FCSTD DOCUMENT  (FreeCAD 0.19R24276 (Git))
Label: v5.6_Full
License: All rights reserved
LicenseURL: http://en.wikipedia.org/wiki/All_rights_reserved
objects: App::Link×7, App::DocumentObjectGroup×2, PartDesign::CoordinateSystem×1, App::FeaturePython×1, App::Part×1
note: 1 computed .brp shape members not serialized (recipe doc carries the construction recipe); baked Part::Feature solids carry a one-line shape summary decoded from their .brp
EXTERNAL_REF file=v5.6_Base.FCStd obj=LCS_Origin
EXTERNAL_REF file=v5.6_Base.FCStd obj=Model
EXTERNAL_REF file=v5.6_Base.FCStd obj=LCS_BaseAssembly_Pivot
EXTERNAL_REF file=v5.6_Primary.FCStd obj=LCS_Pivot
EXTERNAL_REF file=v5.6_Primary.FCStd obj=Model
EXTERNAL_REF file=v5.6_Primary.FCStd obj=LCS_SecondaryAssembly
EXTERNAL_REF file=v5.6_Secondary.FCStd obj=LCS_Origin
EXTERNAL_REF file=v5.6_Secondary.FCStd obj=Model
EXTERNAL_REF file=v5.6_Pole.FCStd obj=LCS_Pole_Bottom
EXTERNAL_REF file=v5.6_Primary.FCStd obj=LCS_Primary_Pole_AP
EXTERNAL_REF file=v5.6_Pole.FCStd obj=Model
EXTERNAL_REF file=v5.6_Pole.FCStd obj=LCS_Pole_Top
EXTERNAL_REF file=v5.6_Primary.FCStd obj=LCS_Primary_Pole_FP

FEATURE [App::DocumentObjectGroup] Parts
FEATURE [PartDesign::CoordinateSystem] LCS_Origin
  AttacherType = Attacher::AttachEngine3D
  MapMode = 2
  Support = -> [X_Axis]
FEATURE [App::DocumentObjectGroup] Constraints
FEATURE [App::FeaturePython] Variables  # WARN: FeaturePython — macro-defined, semantics opaque (R4)
  ZDist = 0
FEATURE [App::Link] v5_6_Base
  AssemblyType = Asm4EE
  AttachedBy = #LCS_Origin
  AttachedTo = Parent Assembly#LCS_Origin
  LinkedObject = -> <external v5.6_Base.FCStd>#Model
  expr: Placement = LCS_Origin.Placement * AttachmentOffset * v5_6_Base#LCS_Origin.Placement ^ -1
FEATURE [App::Link] v5_6_Primary
  AssemblyType = Asm4EE
  AttachedBy = #LCS_Pivot
  AttachedTo = v5_6_Base#LCS_BaseAssembly_Pivot
  LinkPlacement = pos=(0,0,135.2) rot=(0,0,1;0rad)
  LinkedObject = -> <external v5.6_Primary.FCStd>#Model
  Placement = pos=(0,0,135.2) rot=(0,0,1;0rad)
  expr: Placement = v5_6_Base.Placement * v5_6_Base#LCS_BaseAssembly_Pivot.Placement * AttachmentOffset * v5_6_Primary#LCS_Pivot.Placement ^ -1
FEATURE [App::Link] v5_6_Secondary
  AssemblyType = Asm4EE
  AttachedBy = #LCS_Origin
  AttachedTo = v5_6_Primary#LCS_SecondaryAssembly
  LinkPlacement = pos=(0,0,969.2) rot=(0,0,1;0rad)
  LinkedObject = -> <external v5.6_Secondary.FCStd>#Model
  Placement = pos=(0,0,969.2) rot=(0,0,1;0rad)
  expr: Placement = v5_6_Primary.Placement * v5_6_Primary#LCS_SecondaryAssembly.Placement * AttachmentOffset * v5_6_Secondary#LCS_Origin.Placement ^ -1
FEATURE [App::Link] Pole_A1
  AssemblyType = Asm4EE
  AttachedBy = #LCS_Pole_Bottom
  AttachedTo = v5_6_Primary#LCS_Primary_Pole_AP
  LinkPlacement = pos=(113,113,84) rot=(0,0,1;0rad)
  LinkedObject = -> <external v5.6_Pole.FCStd>#Model
  Placement = pos=(113,113,84) rot=(0,0,1;0rad)
  expr: Placement = v5_6_Primary.Placement * v5_6_Primary#LCS_Primary_Pole_AP.Placement * AttachmentOffset * v5_6_Pole#LCS_Pole_Bottom.Placement ^ -1
FEATURE [App::Link] Pole_A2
  AssemblyType = Asm4EE
  AttachedBy = #LCS_Pole_Bottom
  AttachedTo = Pole_A1#LCS_Pole_Top
  LinkPlacement = pos=(113,113,592) rot=(0,0,1;0rad)
  LinkedObject = -> <external v5.6_Pole.FCStd>#Model
  Placement = pos=(113,113,592) rot=(0,0,1;0rad)
  expr: Placement = Pole_A1.Placement * v5_6_Pole#LCS_Pole_Top.Placement * AttachmentOffset * v5_6_Pole#LCS_Pole_Bottom.Placement ^ -1
FEATURE [App::Link] Pole_F1
  AssemblyType = Asm4EE
  AttachedBy = #LCS_Pole_Bottom
  AttachedTo = v5_6_Primary#LCS_Primary_Pole_FP
  LinkPlacement = pos=(113,-113,84) rot=(0,0,1;0rad)
  LinkedObject = -> <external v5.6_Pole.FCStd>#Model
  Placement = pos=(113,-113,84) rot=(0,0,1;0rad)
  expr: Placement = v5_6_Primary.Placement * v5_6_Primary#LCS_Primary_Pole_FP.Placement * AttachmentOffset * v5_6_Pole#LCS_Pole_Bottom.Placement ^ -1
FEATURE [App::Link] Pole_F2
  AssemblyType = Asm4EE
  AttachedBy = #LCS_Pole_Bottom
  AttachedTo = Pole_F1#LCS_Pole_Top
  LinkPlacement = pos=(113,-113,592) rot=(0,0,1;0rad)
  LinkedObject = -> <external v5.6_Pole.FCStd>#Model
  Placement = pos=(113,-113,592) rot=(0,0,1;0rad)
  expr: Placement = Pole_F1.Placement * v5_6_Pole#LCS_Pole_Top.Placement * AttachmentOffset * v5_6_Pole#LCS_Pole_Bottom.Placement ^ -1
FEATURE [App::Part] Model
  Configuration = 0
  Group = -> [LCS_Origin,Constraints,Variables,v5_6_Base,v5_6_Primary,v5_6_Secondary,Pole_A1,Pole_A2,Pole_F1,Pole_F2]
  Origin = -> Origin
  Type = Assembly4 Model

RESOLVED EXTERNAL PARTS (link-assembly join: the EXTERNAL_REF files above that resolve inside this repo's crawl, each included once):
---- part v5.6_Base.FCStd = doc fcstd_4a025d0645c7 ----
FCSTD DOCUMENT  (FreeCAD 0.19R24276 (Git))
Label: v5.6_Base
License: All rights reserved
LicenseURL: http://en.wikipedia.org/wiki/All_rights_reserved
objects: App::Link×37, Part::FeaturePython×32, App::DocumentObjectGroup×2, PartDesign::CoordinateSystem×2, App::FeaturePython×1, App::Part×1
note: 34 computed .brp shape members not serialized (recipe doc carries the construction recipe); baked Part::Feature solids carry a one-line shape summary decoded from their .brp
EXTERNAL_REF file=v5.6_Master.FCStd obj=LCS_AFrame_BaseHub
EXTERNAL_REF file=v5.6_Master.FCStd obj=Part002
EXTERNAL_REF file=v5.6_Master.FCStd obj=LCS_AFrame_Corner_AP
EXTERNAL_REF file=v5.6_Master.FCStd obj=Local_CS097
EXTERNAL_REF file=v5.6_Master.FCStd obj=Body038
EXTERNAL_REF file=v5.6_Master.FCStd obj=LCS_AFrame_Corner_FP
EXTERNAL_REF file=v5.6_Master.FCStd obj=LCS_AFrame_Corner_AS
EXTERNAL_REF file=v5.6_Master.FCStd obj=LCS_AFrame_Corner_FS
EXTERNAL_REF file=v5.6_Master.FCStd obj=LCS_AFrame_Post_AP
EXTERNAL_REF file=v5.6_Master.FCStd obj=Local_CS042
EXTERNAL_REF file=v5.6_Master.FCStd obj=Body018
EXTERNAL_REF file=v5.6_Master.FCStd obj=LCS_AFrame_Post_FP
EXTERNAL_REF file=v5.6_Master.FCStd obj=Local_CS044
EXTERNAL_REF file=v5.6_Master.FCStd obj=LCS_AFrame_Post_AS
EXTERNAL_REF file=v5.6_Master.FCStd obj=LCS_AFrame_Post_FS
EXTERNAL_REF file=v5.6_Master.FCStd obj=Local_CS208
EXTERNAL_REF file=v5.6_Master.FCStd obj=Body022020
EXTERNAL_REF file=v5.6_Master.FCStd obj=Local_CS061
EXTERNAL_REF file=v5.6_Master.FCStd obj=Body020
EXTERNAL_REF file=v5.6_Master.FCStd obj=Local_CS059
EXTERNAL_REF file=v5.6_Master.FCStd obj=Local_CS212
EXTERNAL_REF file=v5.6_Master.FCStd obj=Local_CS217
EXTERNAL_REF file=v5.6_Master.FCStd obj=Body022016
EXTERNAL_REF file=v5.6_Master.FCStd obj=Local_CS213
EXTERNAL_REF file=v5.6_Master.FCStd obj=Local_CS215
EXTERNAL_REF file=v5.6_Master.FCStd obj=Body022017
EXTERNAL_REF file=v5.6_Master.FCStd obj=Local_CS214
EXTERNAL_REF file=v5.6_Master.FCStd obj=Local_CS216
EXTERNAL_REF file=v5.6_Master.FCStd obj=Body022022
EXTERNAL_REF file=v5.6_Master.FCStd obj=Local_CS100
EXTERNAL_REF file=v5.6_Master.FCStd obj=Local_CS108
EXTERNAL_REF file=v5.6_Master.FCStd obj=Body039
EXTERNAL_REF file=v5.6_Master.FCStd obj=Local_CS109
EXTERNAL_REF file=v5.6_Master.FCStd obj=Local_CS111
EXTERNAL_REF file=v5.6_Master.FCStd obj=Local_CS113
EXTERNAL_REF file=v5.6_Master.FCStd obj=Local_CS110
EXTERNAL_REF file=v5.6_Master.FCStd obj=Local_CS112
EXTERNAL_REF file=v5.6_Master.FCStd obj=Local_CS207
EXTERNAL_REF file=v5.6_Master.FCStd obj=Local_CS098
EXTERNAL_REF file=v5.6_Master.FCStd obj=Local_CS099
EXTERNAL_REF file=v5.6_Master.FCStd obj=Local_CS063
EXTERNAL_REF file=v5.6_Master.FCStd obj=Local_CS065
EXTERNAL_REF file=v5.6_Master.FCStd obj=Local_CS182
EXTERNAL_REF file=v5.6_Master.FCStd obj=Local_CS184
EXTERNAL_REF file=v5.6_Master.FCStd obj=Local_CS183
EXTERNAL_REF file=v5.6_Master.FCStd obj=Local_CS185
EXTERNAL_REF file=v5.6_Master.FCStd obj=Local_CS189
EXTERNAL_REF file=v5.6_Master.FCStd obj=Local_CS190
EXTERNAL_REF file=v5.6_Master.FCStd obj=LCS_AFrame_Pivot
EXTERNAL_REF file=v5.6_Master.FCStd obj=Local_CS233
EXTERNAL_REF file=v5.6_Master.FCStd obj=Body022031
EXTERNAL_REF file=v5.6_Master.FCStd obj=Local_CS236
EXTERNAL_REF file=v5.6_Master.FCStd obj=Body003

FEATURE [App::DocumentObjectGroup] Parts
FEATURE [PartDesign::CoordinateSystem] LCS_Origin
  AttacherType = Attacher::AttachEngine3D
  MapMode = 2
  Support = -> [X_Axis]
FEATURE [App::DocumentObjectGroup] Constraints
FEATURE [App::FeaturePython] Variables  # WARN: FeaturePython — macro-defined, semantics opaque (R4)
FEATURE [App::Link] AziFrame
  AssemblyType = Asm4EE
  AttachedBy = #LCS_AFrame_BaseHub
  AttachedTo = Parent Assembly#LCS_Origin
  LinkedObject = -> <external v5.6_Master.FCStd>#Part002
  expr: Placement = LCS_Origin.Placement * AttachmentOffset * v5_6_Master#LCS_AFrame_BaseHub.Placement ^ -1
FEATURE [App::Link] AFrame_Bracket_AP
  AssemblyType = Asm4EE
  AttachedBy = #Local_CS097
  AttachedTo = AziFrame#LCS_AFrame_Corner_AP
  AttachmentOffset = pos=(0,0,0) rot=(0,0,1;3.14159rad)
  LinkPlacement = pos=(115,103,-4e-16) rot=(0,0,1;3.14159rad)
  LinkedObject = -> <external v5.6_Master.FCStd>#Body038
  Placement = pos=(115,103,-4e-16) rot=(0,0,1;3.14159rad)
  expr: Placement = AziFrame.Placement * v5_6_Master#LCS_AFrame_Corner_AP.Placement * AttachmentOffset * v5_6_Master#Local_CS097.Placement ^ -1
FEATURE [App::Link] AFrame_Bracket_FP
  AssemblyType = Asm4EE
  AttachedBy = #Local_CS097
  AttachedTo = AziFrame#LCS_AFrame_Corner_FP
  AttachmentOffset = pos=(0,0,0) rot=(0,0,1;1.5708rad)
  LinkPlacement = pos=(115,-103,-4e-16) rot=(0,0,1;1.5708rad)
  LinkedObject = -> <external v5.6_Master.FCStd>#Body038
  Placement = pos=(115,-103,-4e-16) rot=(0,0,1;1.5708rad)
  expr: Placement = AziFrame.Placement * v5_6_Master#LCS_AFrame_Corner_FP.Placement * AttachmentOffset * v5_6_Master#Local_CS097.Placement ^ -1
FEATURE [App::Link] AFrame_Bracket_AS
  AssemblyType = Asm4EE
  AttachedBy = #Local_CS097
  AttachedTo = AziFrame#LCS_AFrame_Corner_AS
  AttachmentOffset = pos=(0,0,0) rot=(0,0,1;4.71239rad)
  LinkPlacement = pos=(-115,103,-4e-16) rot=(0,0,1;4.71239rad)
  LinkedObject = -> <external v5.6_Master.FCStd>#Body038
  Placement = pos=(-115,103,-4e-16) rot=(0,0,1;4.71239rad)
  expr: Placement = AziFrame.Placement * v5_6_Master#LCS_AFrame_Corner_AS.Placement * AttachmentOffset * v5_6_Master#Local_CS097.Placement ^ -1
FEATURE [App::Link] AFrame_Bracket_FS
  AssemblyType = Asm4EE
  AttachedBy = #Local_CS097
  AttachedTo = AziFrame#LCS_AFrame_Corner_FS
  LinkPlacement = pos=(-115,-103,-4e-16) rot=(0,0,1;0rad)
  LinkedObject = -> <external v5.6_Master.FCStd>#Body038
  Placement = pos=(-115,-103,-4e-16) rot=(0,0,1;0rad)
  expr: Placement = AziFrame.Placement * v5_6_Master#LCS_AFrame_Corner_FS.Placement * AttachmentOffset * v5_6_Master#Local_CS097.Placement ^ -1
FEATURE [App::Link] RockerPost_AP
  AssemblyType = Asm4EE
  AttachedBy = #Local_CS042
  AttachedTo = AziFrame#LCS_AFrame_Post_AP
  AttachmentOffset = pos=(0,0,0) rot=(0.707107,-0.707107,0;3.14159rad)
  LinkPlacement = pos=(128,113,5) rot=(0,0,1;0rad)
  LinkedObject = -> <external v5.6_Master.FCStd>#Body018
  Placement = pos=(128,113,5) rot=(0,0,1;0rad)
  expr: Placement = AziFrame.Placement * v5_6_Master#LCS_AFrame_Post_AP.Placement * AttachmentOffset * v5_6_Master#Local_CS042.Placement ^ -1
FEATURE [App::Link] RockerPost_FP
  AssemblyType = Asm4EE
  AttachedBy = #Local_CS044
  AttachedTo = AziFrame#LCS_AFrame_Post_FP
  AttachmentOffset = pos=(0,0,0) rot=(-0.707107,-0.707107,0;3.14159rad)
  LinkPlacement = pos=(130,-113,5) rot=(0,0,-1;3.14159rad)
  LinkedObject = -> <external v5.6_Master.FCStd>#Body018
  Placement = pos=(130,-113,5) rot=(0,0,-1;3.14159rad)
  expr: Placement = AziFrame.Placement * v5_6_Master#LCS_AFrame_Post_FP.Placement * AttachmentOffset * v5_6_Master#Local_CS044.Placement ^ -1
FEATURE [App::Link] RockerPost_AS
  AssemblyType = Asm4EE
  AttachedBy = #Local_CS044
  AttachedTo = AziFrame#LCS_AFrame_Post_AS
  AttachmentOffset = pos=(0,0,0) rot=(-0.707107,-0.707107,0;3.14159rad)
  LinkPlacement = pos=(-130,113,5) rot=(0,0,1;0rad)
  LinkedObject = -> <external v5.6_Master.FCStd>#Body018
  Placement = pos=(-130,113,5) rot=(0,0,1;0rad)
  expr: Placement = AziFrame.Placement * v5_6_Master#LCS_AFrame_Post_AS.Placement * AttachmentOffset * v5_6_Master#Local_CS044.Placement ^ -1
FEATURE [App::Link] RockerPost_FS
  AssemblyType = Asm4EE
  AttachedBy = #Local_CS042
  AttachedTo = AziFrame#LCS_AFrame_Post_FS
  AttachmentOffset = pos=(0,0,0) rot=(0.707107,-0.707107,0;3.14159rad)
  LinkPlacement = pos=(-128,-113,5) rot=(0,0,1;3.14159rad)
  LinkedObject = -> <external v5.6_Master.FCStd>#Body018
  Placement = pos=(-128,-113,5) rot=(0,0,1;3.14159rad)
  expr: Placement = AziFrame.Placement * v5_6_Master#LCS_AFrame_Post_FS.Placement * AttachmentOffset * v5_6_Master#Local_CS042.Placement ^ -1
FEATURE [App::Link] AzimuthBase
  AssemblyType = Asm4EE
  AttachedBy = #Local_CS208
  AttachedTo = AziFrame#LCS_AFrame_BaseHub
  AttachmentOffset = pos=(0,0,-15) rot=(0,0,1;0rad)
  LinkPlacement = pos=(0,0,-15) rot=(0,0,1;1.5708rad)
  LinkedObject = -> <external v5.6_Master.FCStd>#Body022020
  Placement = pos=(0,0,-15) rot=(0,0,1;1.5708rad)
  expr: Placement = AziFrame.Placement * v5_6_Master#LCS_AFrame_BaseHub.Placement * AttachmentOffset * v5_6_Master#Local_CS208.Placement ^ -1
FEATURE [App::Link] SidePlate_P
  AssemblyType = Asm4EE
  AttachedBy = #Local_CS061
  AttachedTo = RockerPost_AP#Local_CS044
  AttachmentOffset = pos=(0,0,0) rot=(1,0,0;3.14159rad)
  LinkPlacement = pos=(135,-5.68e-14,5) rot=(0,0,1;0rad)
  LinkedObject = -> <external v5.6_Master.FCStd>#Body020
  Placement = pos=(135,-5.68e-14,5) rot=(0,0,1;0rad)
  expr: Placement = RockerPost_AP.Placement * v5_6_Master#Local_CS044.Placement * AttachmentOffset * v5_6_Master#Local_CS061.Placement ^ -1
FEATURE [App::Link] SidePlate_S
  AssemblyType = Asm4EE
  AttachedBy = #Local_CS059
  AttachedTo = RockerPost_AS#Local_CS042
  AttachmentOffset = pos=(0,0,0) rot=(0,1,0;3.14159rad)
  LinkPlacement = pos=(-137,0,5) rot=(0,0,1;0rad)
  LinkedObject = -> <external v5.6_Master.FCStd>#Body020
  Placement = pos=(-137,0,5) rot=(0,0,1;0rad)
  expr: Placement = RockerPost_AS.Placement * v5_6_Master#Local_CS042.Placement * AttachmentOffset * v5_6_Master#Local_CS059.Placement ^ -1
FEATURE [App::Link] ArmSpacer_P
  AssemblyType = Asm4EE
  AttachedBy = #Local_CS212
  AttachedTo = SidePlate_P#Local_CS217
  AttachmentOffset = pos=(0,0,1) rot=(0,0,1;0rad)
  LinkPlacement = pos=(137,-5.98e-14,3.91e-14) rot=(0,0,1;0rad)
  LinkedObject = -> <external v5.6_Master.FCStd>#Body022016
  Placement = pos=(137,-5.98e-14,3.91e-14) rot=(0,0,1;0rad)
  expr: Placement = SidePlate_P.Placement * v5_6_Master#Local_CS217.Placement * AttachmentOffset * v5_6_Master#Local_CS212.Placement ^ -1
FEATURE [App::Link] ArmSpacer_S
  AssemblyType = Asm4EE
  AttachedBy = #Local_CS212
  AttachedTo = SidePlate_S#Local_CS217
  AttachmentOffset = pos=(0,0,-1) rot=(1,0,0;3.14159rad)
  LinkPlacement = pos=(-137,-2.1e-15,-2.96e-14) rot=(0,0,1;3.14159rad)
  LinkedObject = -> <external v5.6_Master.FCStd>#Body022016
  Placement = pos=(-137,-2.1e-15,-2.96e-14) rot=(0,0,1;3.14159rad)
  expr: Placement = SidePlate_S.Placement * v5_6_Master#Local_CS217.Placement * AttachmentOffset * v5_6_Master#Local_CS212.Placement ^ -1
FEATURE [App::Link] ArmPost_P
  AssemblyType = Asm4EE
  AttachedBy = #Local_CS215
  AttachedTo = ArmSpacer_P#Local_CS213
  AttachmentOffset = pos=(0,0,10) rot=(0,0,1;0rad)
  LinkPlacement = pos=(158,-7.99e-14,-10) rot=(0,0,-1;3.14159rad)
  LinkedObject = -> <external v5.6_Master.FCStd>#Body022017
  Placement = pos=(158,-7.99e-14,-10) rot=(0,0,-1;3.14159rad)
  expr: Placement = ArmSpacer_P.Placement * v5_6_Master#Local_CS213.Placement * AttachmentOffset * v5_6_Master#Local_CS215.Placement ^ -1
FEATURE [App::Link] ArmPost_S
  AssemblyType = Asm4EE
  AttachedBy = #Local_CS215
  AttachedTo = ArmSpacer_S#Local_CS213
  AttachmentOffset = pos=(0,0,10) rot=(0,0,1;0rad)
  LinkPlacement = pos=(-158,6.1e-15,-10) rot=(0,0,1;0rad)
  LinkedObject = -> <external v5.6_Master.FCStd>#Body022017
  Placement = pos=(-158,6.1e-15,-10) rot=(0,0,1;0rad)
  expr: Placement = ArmSpacer_S.Placement * v5_6_Master#Local_CS213.Placement * AttachmentOffset * v5_6_Master#Local_CS215.Placement ^ -1
FEATURE [App::Link] ArmBrake_P
  AssemblyType = Asm4EE
  AttachedBy = #Local_CS216
  AttachedTo = ArmPost_P#Local_CS214
  AttachmentOffset = pos=(0,0,18) rot=(0,0,1;0rad)
  LinkPlacement = pos=(159,-2.78e-14,50) rot=(0,0,1;0rad)
  LinkedObject = -> <external v5.6_Master.FCStd>#Body022022
  Placement = pos=(159,-2.78e-14,50) rot=(0,0,1;0rad)
  expr: Placement = ArmPost_P.Placement * v5_6_Master#Local_CS214.Placement * AttachmentOffset * v5_6_Master#Local_CS216.Placement ^ -1
FEATURE [App::Link] ArmBrake_S
  AssemblyType = Asm4EE
  AttachedBy = #Local_CS216
  AttachedTo = ArmPost_S#Local_CS214
  AttachmentOffset = pos=(0,0,18) rot=(0,0,1;0rad)
  LinkPlacement = pos=(-159,1.49e-14,50) rot=(0,0,1;3.14159rad)
  LinkedObject = -> <external v5.6_Master.FCStd>#Body022022
  Placement = pos=(-159,1.49e-14,50) rot=(0,0,1;3.14159rad)
  expr: Placement = ArmPost_S.Placement * v5_6_Master#Local_CS214.Placement * AttachmentOffset * v5_6_Master#Local_CS216.Placement ^ -1
FEATURE [App::Link] AFBracket_AP_TNut_P
  AssemblyType = Asm4EE
  AttachedBy = #Local_CS100
  AttachedTo = AFrame_Bracket_AP#Local_CS108
  LinkPlacement = pos=(116.2,85,1.7e-15) rot=(-0.57735,-0.57735,0.57735;2.0944rad)
  LinkedObject = -> <external v5.6_Master.FCStd>#Body039
  Placement = pos=(116.2,85,1.7e-15) rot=(-0.57735,-0.57735,0.57735;2.0944rad)
  expr: Placement = AFrame_Bracket_AP.Placement * v5_6_Master#Local_CS108.Placement * AttachmentOffset * v5_6_Master#Local_CS100.Placement ^ -1
FEATURE [App::Link] AFBracket_AP_TNut_A
  AssemblyType = Asm4EE
  AttachedBy = #Local_CS100
  AttachedTo = AFrame_Bracket_AP#Local_CS109
  LinkPlacement = pos=(97,104.2,1.5e-15) rot=(0,-0.707107,0.707107;3.14159rad)
  LinkedObject = -> <external v5.6_Master.FCStd>#Body039
  Placement = pos=(97,104.2,1.5e-15) rot=(0,-0.707107,0.707107;3.14159rad)
  expr: Placement = AFrame_Bracket_AP.Placement * v5_6_Master#Local_CS109.Placement * AttachmentOffset * v5_6_Master#Local_CS100.Placement ^ -1
FEATURE [App::Link] AFBracket_FP_TNut_P
  AssemblyType = Asm4EE
  AttachedBy = #Local_CS100
  AttachedTo = AFrame_Bracket_FP#Local_CS109
  LinkPlacement = pos=(116.2,-85,1.4e-15) rot=(-0.57735,-0.57735,0.57735;2.0944rad)
  LinkedObject = -> <external v5.6_Master.FCStd>#Body039
  Placement = pos=(116.2,-85,1.4e-15) rot=(-0.57735,-0.57735,0.57735;2.0944rad)
  expr: Placement = AFrame_Bracket_FP.Placement * v5_6_Master#Local_CS109.Placement * AttachmentOffset * v5_6_Master#Local_CS100.Placement ^ -1
FEATURE [App::Link] AFBracket_FP_TNut_F
  AssemblyType = Asm4EE
  AttachedBy = #Local_CS100
  AttachedTo = AFrame_Bracket_FP#Local_CS108
  LinkPlacement = pos=(97,-104.2,1.6e-15) rot=(-1,0,0;1.5708rad)
  LinkedObject = -> <external v5.6_Master.FCStd>#Body039
  Placement = pos=(97,-104.2,1.6e-15) rot=(-1,0,0;1.5708rad)
  expr: Placement = AFrame_Bracket_FP.Placement * v5_6_Master#Local_CS108.Placement * AttachmentOffset * v5_6_Master#Local_CS100.Placement ^ -1
FEATURE [App::Link] AFBracket_AS_TNut_S
  AssemblyType = Asm4EE
  AttachedBy = #Local_CS100
  AttachedTo = AFrame_Bracket_AS#Local_CS109
  LinkPlacement = pos=(-116.2,85,1.3e-15) rot=(0.57735,-0.57735,0.57735;4.18879rad)
  LinkedObject = -> <external v5.6_Master.FCStd>#Body039
  Placement = pos=(-116.2,85,1.3e-15) rot=(0.57735,-0.57735,0.57735;4.18879rad)
  expr: Placement = AFrame_Bracket_AS.Placement * v5_6_Master#Local_CS109.Placement * AttachmentOffset * v5_6_Master#Local_CS100.Placement ^ -1
FEATURE [App::Link] AFBracket_AS_TNut_A
  AssemblyType = Asm4EE
  AttachedBy = #Local_CS100
  AttachedTo = AFrame_Bracket_AS#Local_CS108
  LinkPlacement = pos=(-97,104.2,1.6e-15) rot=(0,-0.707107,0.707107;3.14159rad)
  LinkedObject = -> <external v5.6_Master.FCStd>#Body039
  Placement = pos=(-97,104.2,1.6e-15) rot=(0,-0.707107,0.707107;3.14159rad)
  expr: Placement = AFrame_Bracket_AS.Placement * v5_6_Master#Local_CS108.Placement * AttachmentOffset * v5_6_Master#Local_CS100.Placement ^ -1
FEATURE [App::Link] AFBracket_FS_TNut_S
  AssemblyType = Asm4EE
  AttachedBy = #Local_CS100
  AttachedTo = AFrame_Bracket_FS#Local_CS108
  LinkPlacement = pos=(-116.2,-85,1.8e-15) rot=(-0.57735,0.57735,-0.57735;2.0944rad)
  LinkedObject = -> <external v5.6_Master.FCStd>#Body039
  Placement = pos=(-116.2,-85,1.8e-15) rot=(-0.57735,0.57735,-0.57735;2.0944rad)
  expr: Placement = AFrame_Bracket_FS.Placement * v5_6_Master#Local_CS108.Placement * AttachmentOffset * v5_6_Master#Local_CS100.Placement ^ -1
FEATURE [App::Link] AFBracket_FS_TNut_A
  AssemblyType = Asm4EE
  AttachedBy = #Local_CS100
  AttachedTo = AFrame_Bracket_FS#Local_CS109
  LinkPlacement = pos=(-97,-104.2,1.5e-15) rot=(-1,0,0;1.5708rad)
  LinkedObject = -> <external v5.6_Master.FCStd>#Body039
  Placement = pos=(-97,-104.2,1.5e-15) rot=(-1,0,0;1.5708rad)
  expr: Placement = AFrame_Bracket_FS.Placement * v5_6_Master#Local_CS109.Placement * AttachmentOffset * v5_6_Master#Local_CS100.Placement ^ -1
FEATURE [App::Link] SidePlate_P_TNut_A
  AssemblyType = Asm4EE
  AttachedBy = #Local_CS100
  AttachedTo = SidePlate_P#Local_CS111
  AttachmentOffset = pos=(0,0,0) rot=(0.707107,-0.707107,0;3.14159rad)
  LinkPlacement = pos=(133.8,83,1.41e-14) rot=(0.57735,0.57735,0.57735;2.0944rad)
  LinkedObject = -> <external v5.6_Master.FCStd>#Body039
  Placement = pos=(133.8,83,1.41e-14) rot=(0.57735,0.57735,0.57735;2.0944rad)
  expr: Placement = SidePlate_P.Placement * v5_6_Master#Local_CS111.Placement * AttachmentOffset * v5_6_Master#Local_CS100.Placement ^ -1
FEATURE [App::Link] SidePlate_P_TNut_F
  AssemblyType = Asm4EE
  AttachedBy = #Local_CS100
  AttachedTo = SidePlate_P#Local_CS113
  AttachmentOffset = pos=(0,0,0) rot=(0.707107,-0.707107,0;3.14159rad)
  LinkPlacement = pos=(133.8,-83,6.56e-14) rot=(0.57735,0.57735,0.57735;2.0944rad)
  LinkedObject = -> <external v5.6_Master.FCStd>#Body039
  Placement = pos=(133.8,-83,6.56e-14) rot=(0.57735,0.57735,0.57735;2.0944rad)
  expr: Placement = SidePlate_P.Placement * v5_6_Master#Local_CS113.Placement * AttachmentOffset * v5_6_Master#Local_CS100.Placement ^ -1
FEATURE [App::Link] SidePlate_S_TNut_A
  AssemblyType = Asm4EE
  AttachedBy = #Local_CS100
  AttachedTo = SidePlate_S#Local_CS110
  AttachmentOffset = pos=(0,0,0) rot=(0.707107,-0.707107,0;3.14159rad)
  LinkPlacement = pos=(-133.8,83,-5.16e-14) rot=(-0.57735,0.57735,0.57735;4.18879rad)
  LinkedObject = -> <external v5.6_Master.FCStd>#Body039
  Placement = pos=(-133.8,83,-5.16e-14) rot=(-0.57735,0.57735,0.57735;4.18879rad)
  expr: Placement = SidePlate_S.Placement * v5_6_Master#Local_CS110.Placement * AttachmentOffset * v5_6_Master#Local_CS100.Placement ^ -1
FEATURE [App::Link] SidePlate_S_TNut_F
  AssemblyType = Asm4EE
  AttachedBy = #Local_CS100
  AttachedTo = SidePlate_S#Local_CS112
  AttachmentOffset = pos=(0,0,0) rot=(0.707107,-0.707107,0;3.14159rad)
  LinkPlacement = pos=(-133.8,-83,-3.6e-15) rot=(-0.57735,0.57735,0.57735;4.18879rad)
  LinkedObject = -> <external v5.6_Master.FCStd>#Body039
  Placement = pos=(-133.8,-83,-3.6e-15) rot=(-0.57735,0.57735,0.57735;4.18879rad)
  expr: Placement = SidePlate_S.Placement * v5_6_Master#Local_CS112.Placement * AttachmentOffset * v5_6_Master#Local_CS100.Placement ^ -1
FEATURE [App::Link] SideBrake_P_TNut_N
  AssemblyType = Asm4EE
  AttachedBy = #Local_CS100
  AttachedTo = ArmSpacer_P#Local_CS212
  AttachmentOffset = pos=(0,0,0) rot=(0,0,1;1.5708rad)
  LinkPlacement = pos=(135.8,-5.92e-14,4.1e-14) rot=(-0.57735,-0.57735,-0.57735;4.18879rad)
  LinkedObject = -> <external v5.6_Master.FCStd>#Body039
  Placement = pos=(135.8,-5.92e-14,4.1e-14) rot=(-0.57735,-0.57735,-0.57735;4.18879rad)
  expr: Placement = ArmSpacer_P.Placement * v5_6_Master#Local_CS212.Placement * AttachmentOffset * v5_6_Master#Local_CS100.Placement ^ -1
FEATURE [App::Link] SideBrake_S_TNut_N
  AssemblyType = Asm4EE
  AttachedBy = #Local_CS100
  AttachedTo = ArmSpacer_S#Local_CS212
  AttachmentOffset = pos=(0,0,0) rot=(0,0,1;1.5708rad)
  LinkPlacement = pos=(-135.8,-2.6e-15,-2.76e-14) rot=(-0.57735,0.57735,0.57735;4.18879rad)
  LinkedObject = -> <external v5.6_Master.FCStd>#Body039
  Placement = pos=(-135.8,-2.6e-15,-2.76e-14) rot=(-0.57735,0.57735,0.57735;4.18879rad)
  expr: Placement = ArmSpacer_S.Placement * v5_6_Master#Local_CS212.Placement * AttachmentOffset * v5_6_Master#Local_CS100.Placement ^ -1
FEATURE [App::Link] SideBrake_P_TNut_Z
  AssemblyType = Asm4EE
  AttachedBy = #Local_CS100
  AttachedTo = ArmPost_P#Local_CS214
  AttachmentOffset = pos=(0,0,10) rot=(0,0,1;0rad)
  LinkPlacement = pos=(166.8,-3.12e-14,50) rot=(0,-1,0;4.71239rad)
  LinkedObject = -> <external v5.6_Master.FCStd>#Body039
  Placement = pos=(166.8,-3.12e-14,50) rot=(0,-1,0;4.71239rad)
  expr: Placement = ArmPost_P.Placement * v5_6_Master#Local_CS214.Placement * AttachmentOffset * v5_6_Master#Local_CS100.Placement ^ -1
FEATURE [App::Link] SideBrake_S_TNut_Z
  AssemblyType = Asm4EE
  AttachedBy = #Local_CS100
  AttachedTo = ArmPost_S#Local_CS214
  AttachmentOffset = pos=(0,0,10) rot=(0,0,1;0rad)
  LinkPlacement = pos=(-166.8,1.76e-14,50) rot=(-0.707107,0,0.707107;3.14159rad)
  LinkedObject = -> <external v5.6_Master.FCStd>#Body039
  Placement = pos=(-166.8,1.76e-14,50) rot=(-0.707107,0,0.707107;3.14159rad)
  expr: Placement = ArmPost_S.Placement * v5_6_Master#Local_CS214.Placement * AttachmentOffset * v5_6_Master#Local_CS100.Placement ^ -1
FEATURE [Part::FeaturePython] Screw  label="M8x55-Screw"  # Fasteners workbench fastener (typed FeaturePython)
  AssemblyType = Asm4EE
  AttachedBy = Origin
  AttachedTo = AzimuthBase#Local_CS207
  AttachmentOffset = pos=(0,0,0) rot=(0,0,1;1.5708rad)
  Placement = pos=(0,0,-26.05) rot=(0.707107,0.707107,0;3.14159rad)
  diameter = 9
  invert = false
  length = 5
  lengthCustom = 55
  matchOuter = false
  offset = 0
  thread = false
  type = 26
  expr: Placement = AzimuthBase.Placement * v5_6_Master#Local_CS207.Placement * AttachmentOffset
FEATURE [Part::FeaturePython] Washer  label="M8-Washer"  # Fasteners workbench fastener (typed FeaturePython)
  AssemblyType = Asm4EE
  AttachedBy = Origin
  AttachedTo = AziFrame#LCS_AFrame_BaseHub
  AttachmentOffset = pos=(0,0,10) rot=(0,0,1;0rad)
  Placement = pos=(0,0,10) rot=(0,0,1;0rad)
  diameter = 6
  invert = false
  matchOuter = false
  offset = 0
  type = 6
  expr: Placement = AziFrame.Placement * v5_6_Master#LCS_AFrame_BaseHub.Placement * AttachmentOffset
FEATURE [Part::FeaturePython] Screw001  label="M5x10-Screw"  # Fasteners workbench fastener (typed FeaturePython)
  AssemblyType = Asm4EE
  AttachedBy = Origin
  AttachedTo = AFrame_Bracket_AP#Local_CS098
  Placement = pos=(110.5,85,3.8e-15) rot=(-0.57735,0.57735,0.57735;4.18879rad)
  diameter = 6
  invert = false
  length = 1
  lengthCustom = 10
  matchOuter = false
  offset = 0
  thread = false
  type = 32
  expr: Placement = AFrame_Bracket_AP.Placement * v5_6_Master#Local_CS098.Placement * AttachmentOffset
FEATURE [Part::FeaturePython] Screw002  label="M5x10-Screw129"  # Fasteners workbench fastener (typed FeaturePython)
  AssemblyType = Asm4EE
  AttachedBy = Origin
  AttachedTo = AFrame_Bracket_AP#Local_CS099
  Placement = pos=(97,98.5,3.3e-15) rot=(-0.57735,-0.57735,0.57735;4.18879rad)
  diameter = 6
  invert = false
  length = 1
  lengthCustom = 10
  matchOuter = false
  offset = 0
  thread = false
  type = 32
  expr: Placement = AFrame_Bracket_AP.Placement * v5_6_Master#Local_CS099.Placement * AttachmentOffset
FEATURE [Part::FeaturePython] Screw003  label="M5x10-Screw130"  # Fasteners workbench fastener (typed FeaturePython)
  AssemblyType = Asm4EE
  AttachedBy = Origin
  AttachedTo = AFrame_Bracket_FP#Local_CS098
  Placement = pos=(97,-98.5,3.8e-15) rot=(0,0.707107,0.707107;3.14159rad)
  diameter = 6
  invert = false
  length = 1
  lengthCustom = 10
  matchOuter = false
  offset = 0
  thread = false
  type = 32
  expr: Placement = AFrame_Bracket_FP.Placement * v5_6_Master#Local_CS098.Placement * AttachmentOffset
FEATURE [Part::FeaturePython] Screw004  label="M5x10-Screw131"  # Fasteners workbench fastener (typed FeaturePython)
  AssemblyType = Asm4EE
  AttachedBy = Origin
  AttachedTo = AFrame_Bracket_FP#Local_CS099
  Placement = pos=(110.5,-85,3.3e-15) rot=(-0.707107,0,0.707107;3.14159rad)
  diameter = 6
  invert = false
  length = 1
  lengthCustom = 10
  matchOuter = false
  offset = 0
  thread = false
  type = 32
  expr: Placement = AFrame_Bracket_FP.Placement * v5_6_Master#Local_CS099.Placement * AttachmentOffset
FEATURE [Part::FeaturePython] Screw005  label="M5x10-Screw132"  # Fasteners workbench fastener (typed FeaturePython)
  AssemblyType = Asm4EE
  AttachedBy = Origin
  AttachedTo = AFrame_Bracket_AS#Local_CS098
  Placement = pos=(-97,98.5,3.8e-15) rot=(-1,0,0;4.71239rad)
  diameter = 6
  invert = false
  length = 1
  lengthCustom = 10
  matchOuter = false
  offset = 0
  thread = false
  type = 32
  expr: Placement = AFrame_Bracket_AS.Placement * v5_6_Master#Local_CS098.Placement * AttachmentOffset
FEATURE [Part::FeaturePython] Screw006  label="M5x10-Screw133"  # Fasteners workbench fastener (typed FeaturePython)
  AssemblyType = Asm4EE
  AttachedBy = Origin
  AttachedTo = AFrame_Bracket_AS#Local_CS099
  Placement = pos=(-110.5,85,3.3e-15) rot=(0,-1,0;4.71239rad)
  diameter = 6
  invert = false
  length = 1
  lengthCustom = 10
  matchOuter = false
  offset = 0
  thread = false
  type = 32
  expr: Placement = AFrame_Bracket_AS.Placement * v5_6_Master#Local_CS099.Placement * AttachmentOffset
FEATURE [Part::FeaturePython] Screw007  label="M5x10-Screw134"  # Fasteners workbench fastener (typed FeaturePython)
  AssemblyType = Asm4EE
  AttachedBy = Origin
  AttachedTo = AFrame_Bracket_FS#Local_CS098
  Placement = pos=(-110.5,-85,3.8e-15) rot=(0.57735,0.57735,0.57735;2.0944rad)
  diameter = 6
  invert = false
  length = 1
  lengthCustom = 10
  matchOuter = false
  offset = 0
  thread = false
  type = 32
  expr: Placement = AFrame_Bracket_FS.Placement * v5_6_Master#Local_CS098.Placement * AttachmentOffset
FEATURE [Part::FeaturePython] Screw008  label="M5x10-Screw135"  # Fasteners workbench fastener (typed FeaturePython)
  AssemblyType = Asm4EE
  AttachedBy = Origin
  AttachedTo = AFrame_Bracket_FS#Local_CS099
  Placement = pos=(-97,-98.5,3.3e-15) rot=(-0.57735,0.57735,0.57735;2.0944rad)
  diameter = 6
  invert = false
  length = 1
  lengthCustom = 10
  matchOuter = false
  offset = 0
  thread = false
  type = 32
  expr: Placement = AFrame_Bracket_FS.Placement * v5_6_Master#Local_CS099.Placement * AttachmentOffset
FEATURE [Part::FeaturePython] Screw009  label="M6x25-Screw"  # Fasteners workbench fastener (typed FeaturePython)
  AssemblyType = Asm4EE
  AttachedBy = Origin
  AttachedTo = SidePlate_P#Local_CS059
  Placement = pos=(137,113,4.4e-15) rot=(-0.707107,0,-0.707107;3.14159rad)
  diameter = 4
  invert = false
  length = 5
  lengthCustom = 25
  matchOuter = false
  offset = 0
  thread = false
  type = 38
  expr: Placement = SidePlate_P.Placement * v5_6_Master#Local_CS059.Placement * AttachmentOffset
FEATURE [Part::FeaturePython] Screw010  label="M6x25-Screw040"  # Fasteners workbench fastener (typed FeaturePython)
  AssemblyType = Asm4EE
  AttachedBy = Origin
  AttachedTo = SidePlate_P#Local_CS063
  Placement = pos=(137,-113,7.55e-14) rot=(-0.707107,0,-0.707107;3.14159rad)
  diameter = 4
  invert = false
  length = 5
  lengthCustom = 25
  matchOuter = false
  offset = 0
  thread = false
  type = 38
  expr: Placement = SidePlate_P.Placement * v5_6_Master#Local_CS063.Placement * AttachmentOffset
FEATURE [Part::FeaturePython] Screw011  label="M6x25-Screw041"  # Fasteners workbench fastener (typed FeaturePython)
  AssemblyType = Asm4EE
  AttachedBy = Origin
  AttachedTo = SidePlate_S#Local_CS061
  Placement = pos=(-137,113,-6.22e-14) rot=(0,1,0;4.71239rad)
  diameter = 4
  invert = false
  length = 5
  lengthCustom = 25
  matchOuter = false
  offset = 0
  thread = false
  type = 38
  expr: Placement = SidePlate_S.Placement * v5_6_Master#Local_CS061.Placement * AttachmentOffset
FEATURE [Part::FeaturePython] Screw012  label="M6x25-Screw042"  # Fasteners workbench fastener (typed FeaturePython)
  AssemblyType = Asm4EE
  AttachedBy = Origin
  AttachedTo = SidePlate_S#Local_CS065
  Placement = pos=(-137,-113,3.6e-15) rot=(0,1,0;4.71239rad)
  diameter = 4
  invert = false
  length = 5
  lengthCustom = 25
  matchOuter = false
  offset = 0
  thread = false
  type = 38
  expr: Placement = SidePlate_S.Placement * v5_6_Master#Local_CS065.Placement * AttachmentOffset
FEATURE [Part::FeaturePython] Screw013  label="M5x8-Screw"  # Fasteners workbench fastener (typed FeaturePython)
  AssemblyType = Asm4EE
  AttachedBy = Origin
  AttachedTo = SidePlate_P#Local_CS110
  Placement = pos=(137,83,1.42e-14) rot=(-0.707107,0,-0.707107;3.14159rad)
  diameter = 6
  invert = false
  length = 0
  lengthCustom = 8
  matchOuter = false
  offset = 0
  thread = false
  type = 32
  expr: Placement = SidePlate_P.Placement * v5_6_Master#Local_CS110.Placement * AttachmentOffset
FEATURE [Part::FeaturePython] Screw014  label="M5x8-Screw049"  # Fasteners workbench fastener (typed FeaturePython)
  AssemblyType = Asm4EE
  AttachedBy = Origin
  AttachedTo = SidePlate_P#Local_CS112
  Placement = pos=(137,-83,6.57e-14) rot=(-0.707107,0,-0.707107;3.14159rad)
  diameter = 6
  invert = false
  length = 0
  lengthCustom = 8
  matchOuter = false
  offset = 0
  thread = false
  type = 32
  expr: Placement = SidePlate_P.Placement * v5_6_Master#Local_CS112.Placement * AttachmentOffset
FEATURE [Part::FeaturePython] Screw015  label="M5x8-Screw050"  # Fasteners workbench fastener (typed FeaturePython)
  AssemblyType = Asm4EE
  AttachedBy = Origin
  AttachedTo = SidePlate_S#Local_CS111
  Placement = pos=(-137,83,-5.33e-14) rot=(0,1,0;4.71239rad)
  diameter = 6
  invert = false
  length = 0
  lengthCustom = 8
  matchOuter = false
  offset = 0
  thread = false
  type = 32
  expr: Placement = SidePlate_S.Placement * v5_6_Master#Local_CS111.Placement * AttachmentOffset
FEATURE [Part::FeaturePython] Screw016  label="M5x8-Screw051"  # Fasteners workbench fastener (typed FeaturePython)
  AssemblyType = Asm4EE
  AttachedBy = Origin
  AttachedTo = SidePlate_S#Local_CS113
  Placement = pos=(-137,-83,-5.3e-15) rot=(0,1,0;4.71239rad)
  diameter = 6
  invert = false
  length = 0
  lengthCustom = 8
  matchOuter = false
  offset = 0
  thread = false
  type = 32
  expr: Placement = SidePlate_S.Placement * v5_6_Master#Local_CS113.Placement * AttachmentOffset
FEATURE [Part::FeaturePython] Screw017  label="M5x20-Screw"  # Fasteners workbench fastener (typed FeaturePython)
  AssemblyType = Asm4EE
  AttachedBy = Origin
  AttachedTo = SidePlate_P#Local_CS182
  Placement = pos=(137,113,30) rot=(-0.707107,0,-0.707107;3.14159rad)
  diameter = 6
  invert = false
  length = 5
  lengthCustom = 20
  matchOuter = false
  offset = 0
  thread = false
  type = 32
  expr: Placement = SidePlate_P.Placement * v5_6_Master#Local_CS182.Placement * AttachmentOffset
FEATURE [Part::FeaturePython] Screw018  label="M5x20-Screw087"  # Fasteners workbench fastener (typed FeaturePython)
  AssemblyType = Asm4EE
  AttachedBy = Origin
  AttachedTo = SidePlate_P#Local_CS184
  Placement = pos=(137,-113,30) rot=(-0.707107,0,-0.707107;3.14159rad)
  diameter = 6
  invert = false
  length = 5
  lengthCustom = 20
  matchOuter = false
  offset = 0
  thread = false
  type = 32
  expr: Placement = SidePlate_P.Placement * v5_6_Master#Local_CS184.Placement * AttachmentOffset
FEATURE [Part::FeaturePython] Screw019  label="M5x20-Screw088"  # Fasteners workbench fastener (typed FeaturePython)
  AssemblyType = Asm4EE
  AttachedBy = Origin
  AttachedTo = SidePlate_S#Local_CS183
  Placement = pos=(-137,113,30) rot=(0,1,0;4.71239rad)
  diameter = 6
  invert = false
  length = 5
  lengthCustom = 20
  matchOuter = false
  offset = 0
  thread = false
  type = 32
  expr: Placement = SidePlate_S.Placement * v5_6_Master#Local_CS183.Placement * AttachmentOffset
FEATURE [Part::FeaturePython] Screw020  label="M5x20-Screw089"  # Fasteners workbench fastener (typed FeaturePython)
  AssemblyType = Asm4EE
  AttachedBy = Origin
  AttachedTo = SidePlate_S#Local_CS185
  Placement = pos=(-137,-113,30) rot=(0,1,0;4.71239rad)
  diameter = 6
  invert = false
  length = 5
  lengthCustom = 20
  matchOuter = false
  offset = 0
  thread = false
  type = 32
  expr: Placement = SidePlate_S.Placement * v5_6_Master#Local_CS185.Placement * AttachmentOffset
FEATURE [Part::FeaturePython] Washer001  label="M5-Washer"  # Fasteners workbench fastener (typed FeaturePython)
  AssemblyType = Asm4EE
  AttachedBy = Origin
  AttachedTo = RockerPost_AP#Local_CS189
  Placement = pos=(123,113,30) rot=(0.707107,0,-0.707107;3.14159rad)
  diameter = 6
  invert = false
  matchOuter = false
  offset = 0
  type = 3
  expr: Placement = RockerPost_AP.Placement * v5_6_Master#Local_CS189.Placement * AttachmentOffset
FEATURE [Part::FeaturePython] Washer002  label="M5-Washer049"  # Fasteners workbench fastener (typed FeaturePython)
  AssemblyType = Asm4EE
  AttachedBy = Origin
  AttachedTo = RockerPost_FP#Local_CS190
  Placement = pos=(123,-113,30) rot=(0,-1,0;1.5708rad)
  diameter = 6
  invert = false
  matchOuter = false
  offset = 0
  type = 3
  expr: Placement = RockerPost_FP.Placement * v5_6_Master#Local_CS190.Placement * AttachmentOffset
FEATURE [Part::FeaturePython] Washer003  label="M5-Washer050"  # Fasteners workbench fastener (typed FeaturePython)
  AssemblyType = Asm4EE
  AttachedBy = Origin
  AttachedTo = RockerPost_AS#Local_CS190
  Placement = pos=(-123,113,30) rot=(0.707107,0,0.707107;3.14159rad)
  diameter = 6
  invert = false
  matchOuter = false
  offset = 0
  type = 3
  expr: Placement = RockerPost_AS.Placement * v5_6_Master#Local_CS190.Placement * AttachmentOffset
FEATURE [Part::FeaturePython] Washer004  label="M5-Washer051"  # Fasteners workbench fastener (typed FeaturePython)
  AssemblyType = Asm4EE
  AttachedBy = Origin
  AttachedTo = RockerPost_FS#Local_CS189
  Placement = pos=(-123,-113,30) rot=(0,1,0;1.5708rad)
  diameter = 6
  invert = false
  matchOuter = false
  offset = 0
  type = 3
  expr: Placement = RockerPost_FS.Placement * v5_6_Master#Local_CS189.Placement * AttachmentOffset
FEATURE [Part::FeaturePython] Nut001  label="M5-Nut"  # Fasteners workbench fastener (typed FeaturePython)
  AssemblyType = Asm4EE
  AttachedBy = Origin
  AttachedTo = RockerPost_AP#Local_CS189
  AttachmentOffset = pos=(0,0,1) rot=(0,0,1;0rad)
  Placement = pos=(122,113,30) rot=(0.707107,0,-0.707107;3.14159rad)
  diameter = 7
  invert = false
  matchOuter = false
  offset = 0
  thread = false
  type = 7
  expr: Placement = RockerPost_AP.Placement * v5_6_Master#Local_CS189.Placement * AttachmentOffset
FEATURE [Part::FeaturePython] Nut002  label="M5-Nut049"  # Fasteners workbench fastener (typed FeaturePython)
  AssemblyType = Asm4EE
  AttachedBy = Origin
  AttachedTo = RockerPost_FP#Local_CS190
  AttachmentOffset = pos=(0,0,1) rot=(0,0,1;0rad)
  Placement = pos=(122,-113,30) rot=(0,-1,0;1.5708rad)
  diameter = 7
  invert = false
  matchOuter = false
  offset = 0
  thread = false
  type = 7
  expr: Placement = RockerPost_FP.Placement * v5_6_Master#Local_CS190.Placement * AttachmentOffset
FEATURE [Part::FeaturePython] Nut003  label="M5-Nut050"  # Fasteners workbench fastener (typed FeaturePython)
  AssemblyType = Asm4EE
  AttachedBy = Origin
  AttachedTo = RockerPost_AS#Local_CS190
  AttachmentOffset = pos=(0,0,1) rot=(0,0,1;0rad)
  Placement = pos=(-122,113,30) rot=(0.707107,0,0.707107;3.14159rad)
  diameter = 7
  invert = false
  matchOuter = false
  offset = 0
  thread = false
  type = 7
  expr: Placement = RockerPost_AS.Placement * v5_6_Master#Local_CS190.Placement * AttachmentOffset
FEATURE [Part::FeaturePython] Nut004  label="M5-Nut051"  # Fasteners workbench fastener (typed FeaturePython)
  AssemblyType = Asm4EE
  AttachedBy = Origin
  AttachedTo = RockerPost_FS#Local_CS189
  AttachmentOffset = pos=(0,0,1) rot=(0,0,1;0rad)
  Placement = pos=(-122,-113,30) rot=(0,1,0;1.5708rad)
  diameter = 7
  invert = false
  matchOuter = false
  offset = 0
  thread = false
  type = 7
  expr: Placement = RockerPost_FS.Placement * v5_6_Master#Local_CS189.Placement * AttachmentOffset
FEATURE [Part::FeaturePython] Screw021  label="M5x20-Screw090"  # Fasteners workbench fastener (typed FeaturePython)
  AssemblyType = Asm4EE
  AttachedBy = Origin
  AttachedTo = ArmPost_P#Local_CS215
  AttachmentOffset = pos=(0,0,-8) rot=(0,0,1;0rad)
  Placement = pos=(150,-6.69e-14,4.17e-14) rot=(-0.707107,0,-0.707107;3.14159rad)
  diameter = 3
  invert = false
  length = 5
  lengthCustom = 20
  matchOuter = false
  offset = 0
  thread = false
  type = 38
  expr: Placement = ArmPost_P.Placement * v5_6_Master#Local_CS215.Placement * AttachmentOffset
FEATURE [Part::FeaturePython] Screw022  label="M5x20-Screw091"  # Fasteners workbench fastener (typed FeaturePython)
  AssemblyType = Asm4EE
  AttachedBy = Origin
  AttachedTo = ArmPost_S#Local_CS215
  AttachmentOffset = pos=(0,0,-8) rot=(0,0,1;0rad)
  Placement = pos=(-150,3.9e-15,-2.93e-14) rot=(0,1,0;4.71239rad)
  diameter = 3
  invert = false
  length = 5
  lengthCustom = 20
  matchOuter = false
  offset = 0
  thread = false
  type = 38
  expr: Placement = ArmPost_S.Placement * v5_6_Master#Local_CS215.Placement * AttachmentOffset
FEATURE [PartDesign::CoordinateSystem] LCS_BaseAssembly_Pivot
  AttacherType = Attacher::AttachEngine3D
  Placement = pos=(0,0,215) rot=(0,0,1;0rad)
  expr: Placement = AziFrame.Placement * v5_6_Master#LCS_AFrame_Pivot.Placement * AttachmentOffset
FEATURE [App::Link] BaseBolt
  AssemblyType = Asm4EE
  AttachedBy = #Local_CS233
  AttachedTo = AziFrame#LCS_AFrame_BaseHub
  AttachmentOffset = pos=(0,0,14) rot=(0,0,1;0rad)
  LinkPlacement = pos=(0,0,14) rot=(0,0,-1;1.5708rad)
  LinkedObject = -> <external v5.6_Master.FCStd>#Body022031
  Placement = pos=(0,0,14) rot=(0,0,-1;1.5708rad)
  expr: Placement = AziFrame.Placement * v5_6_Master#LCS_AFrame_BaseHub.Placement * AttachmentOffset * v5_6_Master#Local_CS233.Placement ^ -1
FEATURE [App::Link] SideArm_P_Knob
  AssemblyType = Asm4EE
  AttachedBy = #Local_CS236
  AttachedTo = ArmBrake_P#Local_CS216
  LinkPlacement = pos=(176,-3.53e-14,50) rot=(-0.57735,-0.57735,-0.57735;4.18879rad)
  LinkedObject = -> <external v5.6_Master.FCStd>#Body003
  Placement = pos=(176,-3.53e-14,50) rot=(-0.57735,-0.57735,-0.57735;4.18879rad)
  expr: Placement = ArmBrake_P.Placement * v5_6_Master#Local_CS216.Placement * AttachmentOffset * v5_6_Master#Local_CS236.Placement ^ -1
FEATURE [App::Link] SideArm_S_Knob
  AssemblyType = Asm4EE
  AttachedBy = #Local_CS236
  AttachedTo = ArmBrake_S#Local_CS216
  LinkPlacement = pos=(-176,2.09e-14,50) rot=(-0.57735,0.57735,0.57735;4.18879rad)
  LinkedObject = -> <external v5.6_Master.FCStd>#Body003
  Placement = pos=(-176,2.09e-14,50) rot=(-0.57735,0.57735,0.57735;4.18879rad)
  expr: Placement = ArmBrake_S.Placement * v5_6_Master#Local_CS216.Placement * AttachmentOffset * v5_6_Master#Local_CS236.Placement ^ -1
FEATURE [App::Part] Model  label="Base"
  Configuration = 0
  Group = -> [LCS_Origin,Constraints,Variables,AziFrame,AFrame_Bracket_AP,AFrame_Bracket_FP,AFrame_Bracket_AS,AFrame_Bracket_FS,RockerPost_AP,RockerPost_FP,RockerPost_AS,RockerPost_FS,AzimuthBase,SidePlate_P,SidePlate_S,ArmSpacer_P,ArmSpacer_S,ArmPost_P,ArmPost_S,ArmBrake_P,ArmBrake_S,AFBracket_AP_TNut_P,AFBracket_AP_TNut_A,AFBracket_FP_TNut_P,AFBracket_FP_TNut_F,AFBracket_AS_TNut_S,AFBracket_AS_TNut_A,+46 more]
  Origin = -> Origin
  Type = Assembly4 Model
---- part v5.6_Pole.FCStd = doc fcstd_95a1a458b2c4 ----
FCSTD DOCUMENT  (FreeCAD 0.19R24276 (Git))
Label: v5.6_Pole
License: All rights reserved
LicenseURL: http://en.wikipedia.org/wiki/All_rights_reserved
objects: PartDesign::CoordinateSystem×3, App::Link×3, App::DocumentObjectGroup×2, Part::FeaturePython×2, App::FeaturePython×1, App::Part×1
note: 5 computed .brp shape members not serialized (recipe doc carries the construction recipe); baked Part::Feature solids carry a one-line shape summary decoded from their .brp
EXTERNAL_REF file=v5.6_Master.FCStd obj=Local_CS040
EXTERNAL_REF file=v5.6_Master.FCStd obj=Body015
EXTERNAL_REF file=v5.6_Master.FCStd obj=Local_CS204
EXTERNAL_REF file=v5.6_Master.FCStd obj=Body022015
EXTERNAL_REF file=v5.6_Master.FCStd obj=Local_CS199
EXTERNAL_REF file=v5.6_Master.FCStd obj=Local_CS202
EXTERNAL_REF file=v5.6_Master.FCStd obj=Local_CS203

FEATURE [App::DocumentObjectGroup] Parts
FEATURE [PartDesign::CoordinateSystem] LCS_Origin
  AttacherType = Attacher::AttachEngine3D
  MapMode = 2
  Support = -> [X_Axis]
FEATURE [App::DocumentObjectGroup] Constraints
FEATURE [App::FeaturePython] Variables  # WARN: FeaturePython — macro-defined, semantics opaque (R4)
FEATURE [App::Link] Pole_Body
  AssemblyType = Asm4EE
  AttachedBy = #Local_CS040
  AttachedTo = Parent Assembly#LCS_Origin
  LinkPlacement = pos=(0,0,0) rot=(0,0,-1;1.5708rad)
  LinkedObject = -> <external v5.6_Master.FCStd>#Body015
  Placement = pos=(0,0,0) rot=(0,0,-1;1.5708rad)
  expr: Placement = LCS_Origin.Placement * AttachmentOffset * v5_6_Master#Local_CS040.Placement ^ -1
FEATURE [App::Link] PoleBase_Lower
  AssemblyType = Asm4EE
  AttachedBy = #Local_CS204
  AttachedTo = Pole_Body#Local_CS040
  LinkPlacement = pos=(0,0,-4) rot=(0,0,-1;1.5708rad)
  LinkedObject = -> <external v5.6_Master.FCStd>#Body022015
  Placement = pos=(0,0,-4) rot=(0,0,-1;1.5708rad)
  expr: Placement = Pole_Body.Placement * v5_6_Master#Local_CS040.Placement * AttachmentOffset * v5_6_Master#Local_CS204.Placement ^ -1
FEATURE [App::Link] PoleBase_Upper
  AssemblyType = Asm4EE
  AttachedBy = #Local_CS204
  AttachedTo = Pole_Body#Local_CS199
  LinkPlacement = pos=(0,0,504) rot=(0.707107,-0.707107,0;3.14159rad)
  LinkedObject = -> <external v5.6_Master.FCStd>#Body022015
  Placement = pos=(0,0,504) rot=(0.707107,-0.707107,0;3.14159rad)
  expr: Placement = Pole_Body.Placement * v5_6_Master#Local_CS199.Placement * AttachmentOffset * v5_6_Master#Local_CS204.Placement ^ -1
FEATURE [Part::FeaturePython] Screw  label="M5x20-Screw"  # Fasteners workbench fastener (typed FeaturePython)
  AssemblyType = Asm4EE
  AttachedBy = Origin
  AttachedTo = PoleBase_Lower#Local_CS202
  Placement = pos=(0,0,0) rot=(0,0,1;1.5708rad)
  diameter = 7
  invert = false
  length = 5
  lengthCustom = 20
  matchOuter = false
  offset = 0
  thread = false
  type = 27
  expr: Placement = PoleBase_Lower.Placement * v5_6_Master#Local_CS202.Placement * AttachmentOffset
FEATURE [Part::FeaturePython] Nut  label="M5-Nut"  # Fasteners workbench fastener (typed FeaturePython)
  AssemblyType = Asm4EE
  AttachedBy = Origin
  AttachedTo = PoleBase_Upper#Local_CS202
  Placement = pos=(0,0,500) rot=(-0.707107,-0.707107,0;3.14159rad)
  diameter = 7
  invert = false
  matchOuter = false
  offset = 0
  thread = false
  type = 7
  expr: Placement = PoleBase_Upper.Placement * v5_6_Master#Local_CS202.Placement * AttachmentOffset
FEATURE [PartDesign::CoordinateSystem] LCS_Pole_Bottom
  AttacherType = Attacher::AttachEngine3D
  Placement = pos=(0,0,-4) rot=(0,0,1;0rad)
  expr: Placement = PoleBase_Lower.Placement * v5_6_Master#Local_CS203.Placement * AttachmentOffset
FEATURE [PartDesign::CoordinateSystem] LCS_Pole_Top
  AttacherType = Attacher::AttachEngine3D
  AttachmentOffset = pos=(0,0,0) rot=(0,-1,0;3.14159rad)
  Placement = pos=(0,0,504) rot=(0,0,1;0rad)
  expr: Placement = PoleBase_Upper.Placement * v5_6_Master#Local_CS203.Placement * AttachmentOffset
FEATURE [App::Part] Model  label="Pole"
  Configuration = 0
  Group = -> [LCS_Origin,Constraints,Variables,Pole_Body,PoleBase_Lower,PoleBase_Upper,Screw,Nut,LCS_Pole_Bottom,LCS_Pole_Top]
  Origin = -> Origin
  Type = Assembly4 Model
---- part v5.6_Primary.FCStd = doc fcstd_4a564404a3ed ----
FCSTD DOCUMENT  (FreeCAD 0.19R24276 (Git))
Label: v5.6_Primary
License: All rights reserved
LicenseURL: http://en.wikipedia.org/wiki/All_rights_reserved
objects: App::Link×38, Part::FeaturePython×36, PartDesign::CoordinateSystem×7, App::DocumentObjectGroup×2, App::FeaturePython×1, App::Part×1
note: 43 computed .brp shape members not serialized (recipe doc carries the construction recipe); baked Part::Feature solids carry a one-line shape summary decoded from their .brp
EXTERNAL_REF file=v5.6_Master.FCStd obj=Local_CS
EXTERNAL_REF file=v5.6_Master.FCStd obj=Body014
EXTERNAL_REF file=v5.6_Master.FCStd obj=Local_CS001
EXTERNAL_REF file=v5.6_Master.FCStd obj=Local_CS005
EXTERNAL_REF file=v5.6_Master.FCStd obj=Body
EXTERNAL_REF file=v5.6_Master.FCStd obj=Local_CS002
EXTERNAL_REF file=v5.6_Master.FCStd obj=Local_CS006
EXTERNAL_REF file=v5.6_Master.FCStd obj=Body002
EXTERNAL_REF file=v5.6_Master.FCStd obj=Local_CS007
EXTERNAL_REF file=v5.6_Master.FCStd obj=Local_CS008
EXTERNAL_REF file=v5.6_Master.FCStd obj=LCS_LowerCell_Float_X
EXTERNAL_REF file=v5.6_Master.FCStd obj=Local_CS012
EXTERNAL_REF file=v5.6_Master.FCStd obj=Part
EXTERNAL_REF file=v5.6_Master.FCStd obj=LCS_LowerCell_RockerHole_P
EXTERNAL_REF file=v5.6_Master.FCStd obj=Local_CS024
EXTERNAL_REF file=v5.6_Master.FCStd obj=Body006
EXTERNAL_REF file=v5.6_Master.FCStd obj=LCS_LowerCell_RockerHole_S
EXTERNAL_REF file=v5.6_Master.FCStd obj=Local_CS028
EXTERNAL_REF file=v5.6_Master.FCStd obj=LCS_LowerCell_BCorner_AP
EXTERNAL_REF file=v5.6_Master.FCStd obj=Local_CS097
EXTERNAL_REF file=v5.6_Master.FCStd obj=Body038
EXTERNAL_REF file=v5.6_Master.FCStd obj=LCS_LowerCell_BCorner_AS
EXTERNAL_REF file=v5.6_Master.FCStd obj=LCS_LowerCell_CollPoint_F
EXTERNAL_REF file=v5.6_Master.FCStd obj=Local_CS191
EXTERNAL_REF file=v5.6_Master.FCStd obj=Body022010
EXTERNAL_REF file=v5.6_Master.FCStd obj=LCS_LowerCell_CollPoint_AP
EXTERNAL_REF file=v5.6_Master.FCStd obj=LCS_LowerCell_CollPoint_AS
EXTERNAL_REF file=v5.6_Master.FCStd obj=Local_CS081
EXTERNAL_REF file=v5.6_Master.FCStd obj=Local_CS086
EXTERNAL_REF file=v5.6_Master.FCStd obj=Body022
EXTERNAL_REF file=v5.6_Master.FCStd obj=Local_CS082
EXTERNAL_REF file=v5.6_Master.FCStd obj=Local_CS080
EXTERNAL_REF file=v5.6_Master.FCStd obj=Local_CS083
EXTERNAL_REF file=v5.6_Master.FCStd obj=Local_CS100
EXTERNAL_REF file=v5.6_Master.FCStd obj=Body039
EXTERNAL_REF file=v5.6_Master.FCStd obj=Local_CS026
EXTERNAL_REF file=v5.6_Master.FCStd obj=Local_CS030
EXTERNAL_REF file=v5.6_Master.FCStd obj=Local_CS108
EXTERNAL_REF file=v5.6_Master.FCStd obj=Local_CS109
EXTERNAL_REF file=v5.6_Master.FCStd obj=Local_CS009
EXTERNAL_REF file=v5.6_Master.FCStd obj=Local_CS114
EXTERNAL_REF file=v5.6_Master.FCStd obj=Local_CS115
EXTERNAL_REF file=v5.6_Master.FCStd obj=Local_CS116
EXTERNAL_REF file=v5.6_Master.FCStd obj=Local_CS117
EXTERNAL_REF file=v5.6_Master.FCStd obj=Local_CS118
EXTERNAL_REF file=v5.6_Master.FCStd obj=Local_CS119
EXTERNAL_REF file=v5.6_Master.FCStd obj=Local_CS120
EXTERNAL_REF file=v5.6_Master.FCStd obj=Local_CS121
EXTERNAL_REF file=v5.6_Master.FCStd obj=Local_CS098
EXTERNAL_REF file=v5.6_Master.FCStd obj=Local_CS099
EXTERNAL_REF file=v5.6_Master.FCStd obj=LCS_LowerCell_Pole_AP
EXTERNAL_REF file=v5.6_Master.FCStd obj=LCS_LowerCell_Pole_FP
EXTERNAL_REF file=v5.6_Master.FCStd obj=LCS_LowerCell_Pivot_X
EXTERNAL_REF file=v5.6_Master.FCStd obj=Local_CS039
EXTERNAL_REF file=v5.6_Master.FCStd obj=LCS_LowerCell_Pole_AS
EXTERNAL_REF file=v5.6_Master.FCStd obj=LCS_LowerCell_Pole_FS
EXTERNAL_REF file=v5.6_Master.FCStd obj=Local_CS011
EXTERNAL_REF file=v5.6_Master.FCStd obj=Local_CS010
EXTERNAL_REF file=v5.6_Master.FCStd obj=LCS_LowerCell_Counterweight
EXTERNAL_REF file=v5.6_Master.FCStd obj=Local_CS209
EXTERNAL_REF file=v5.6_Master.FCStd obj=Body022019
EXTERNAL_REF file=v5.6_Master.FCStd obj=Local_CS210
EXTERNAL_REF file=v5.6_Master.FCStd obj=Local_CS211
EXTERNAL_REF file=v5.6_Master.FCStd obj=Local_CS218
EXTERNAL_REF file=v5.6_Master.FCStd obj=Body017
EXTERNAL_REF file=v5.6_Master.FCStd obj=Local_CS087
EXTERNAL_REF file=v5.6_Master.FCStd obj=Local_CS088
EXTERNAL_REF file=v5.6_Master.FCStd obj=Local_CS235
EXTERNAL_REF file=v5.6_Master.FCStd obj=Body022032
EXTERNAL_REF file=v5.6_Master.FCStd obj=Local_CS234
EXTERNAL_REF file=v5.6_Master.FCStd obj=Body022030

FEATURE [App::DocumentObjectGroup] Parts
FEATURE [PartDesign::CoordinateSystem] LCS_Origin
  AttacherType = Attacher::AttachEngine3D
  MapMode = 2
  Support = -> [X_Axis]
FEATURE [App::DocumentObjectGroup] Constraints
FEATURE [App::FeaturePython] Variables  # WARN: FeaturePython — macro-defined, semantics opaque (R4)
FEATURE [App::Link] PrimaryMirror
  AssemblyType = Asm4EE
  AttachedBy = #Local_CS
  AttachedTo = Parent Assembly#LCS_Origin
  LinkedObject = -> <external v5.6_Master.FCStd>#Body014
  expr: Placement = LCS_Origin.Placement * AttachmentOffset * v5_6_Master#Local_CS.Placement ^ -1
FEATURE [App::Link] UpperCell
  AssemblyType = Asm4EE
  AttachedBy = #Local_CS005
  AttachedTo = PrimaryMirror#Local_CS001
  AttachmentOffset = pos=(0,0,0) rot=(0,0,1;1.5708rad)
  LinkPlacement = pos=(0,0,-37) rot=(0,0,1;0rad)
  LinkedObject = -> <external v5.6_Master.FCStd>#Body
  Placement = pos=(0,0,-37) rot=(0,0,1;0rad)
  expr: Placement = PrimaryMirror.Placement * v5_6_Master#Local_CS001.Placement * AttachmentOffset * v5_6_Master#Local_CS005.Placement ^ -1
FEATURE [App::Link] LowerPad_A
  AssemblyType = Asm4EE
  AttachedBy = #Local_CS002
  AttachedTo = UpperCell#Local_CS006
  LinkPlacement = pos=(0,60,-31) rot=(0,0,-1;1.5708rad)
  LinkedObject = -> <external v5.6_Master.FCStd>#Body002
  Placement = pos=(0,60,-31) rot=(0,0,-1;1.5708rad)
  expr: Placement = UpperCell.Placement * v5_6_Master#Local_CS006.Placement * AttachmentOffset * v5_6_Master#Local_CS002.Placement ^ -1
FEATURE [App::Link] LowerPad_FP
  AssemblyType = Asm4EE
  AttachedBy = #Local_CS002
  AttachedTo = UpperCell#Local_CS007
  LinkPlacement = pos=(51.9615,-30,-31) rot=(0,0,-1;3.66519rad)
  LinkedObject = -> <external v5.6_Master.FCStd>#Body002
  Placement = pos=(51.9615,-30,-31) rot=(0,0,-1;3.66519rad)
  expr: Placement = UpperCell.Placement * v5_6_Master#Local_CS007.Placement * AttachmentOffset * v5_6_Master#Local_CS002.Placement ^ -1
FEATURE [App::Link] LowerPad_FS
  AssemblyType = Asm4EE
  AttachedBy = #Local_CS002
  AttachedTo = UpperCell#Local_CS008
  LinkPlacement = pos=(-51.9615,-30,-31) rot=(0,0,1;0.523599rad)
  LinkedObject = -> <external v5.6_Master.FCStd>#Body002
  Placement = pos=(-51.9615,-30,-31) rot=(0,0,1;0.523599rad)
  expr: Placement = UpperCell.Placement * v5_6_Master#Local_CS008.Placement * AttachmentOffset * v5_6_Master#Local_CS002.Placement ^ -1
FEATURE [App::Link] LowerCell
  AssemblyType = Asm4EE
  AttachedBy = #LCS_LowerCell_Float_X
  AttachedTo = UpperCell#Local_CS012
  AttachmentOffset = pos=(0,0,0) rot=(0,0,1;4.71239rad)
  LinkPlacement = pos=(0,0,-65.2) rot=(0,0,1;0rad)
  LinkedObject = -> <external v5.6_Master.FCStd>#Part
  Placement = pos=(0,0,-65.2) rot=(0,0,1;0rad)
  expr: Placement = UpperCell.Placement * v5_6_Master#Local_CS012.Placement * AttachmentOffset * v5_6_Master#LCS_LowerCell_Float_X.Placement ^ -1
FEATURE [App::Link] Rocker_P
  AssemblyType = Asm4EE
  AttachedBy = #Local_CS024
  AttachedTo = LowerCell#LCS_LowerCell_RockerHole_P
  AttachmentOffset = pos=(0,0,0) rot=(0,1,0;3.14159rad)
  LinkPlacement = pos=(128,-7.11e-14,79.8) rot=(0,0,1;0rad)
  LinkedObject = -> <external v5.6_Master.FCStd>#Body006
  Placement = pos=(128,-7.11e-14,79.8) rot=(0,0,1;0rad)
  expr: Placement = LowerCell.Placement * v5_6_Master#LCS_LowerCell_RockerHole_P.Placement * AttachmentOffset * v5_6_Master#Local_CS024.Placement ^ -1
FEATURE [App::Link] Rocker_S
  AssemblyType = Asm4EE
  AttachedBy = #Local_CS028
  AttachedTo = LowerCell#LCS_LowerCell_RockerHole_S
  AttachmentOffset = pos=(0,0,0) rot=(1,0,0;3.14159rad)
  LinkPlacement = pos=(-128,5.68e-14,79.8) rot=(0,0,1;0rad)
  LinkedObject = -> <external v5.6_Master.FCStd>#Body006
  Placement = pos=(-128,5.68e-14,79.8) rot=(0,0,1;0rad)
  expr: Placement = LowerCell.Placement * v5_6_Master#LCS_LowerCell_RockerHole_S.Placement * AttachmentOffset * v5_6_Master#Local_CS028.Placement ^ -1
FEATURE [App::Link] LCFrame_Bracket_AP
  AssemblyType = Asm4EE
  AttachedBy = #Local_CS097
  AttachedTo = LowerCell#LCS_LowerCell_BCorner_AP
  AttachmentOffset = pos=(0,0,0) rot=(0,0,1;3.14159rad)
  LinkPlacement = pos=(103,82,-65.2) rot=(0,0,-1;3.14159rad)
  LinkedObject = -> <external v5.6_Master.FCStd>#Body038
  Placement = pos=(103,82,-65.2) rot=(0,0,-1;3.14159rad)
  expr: Placement = LowerCell.Placement * v5_6_Master#LCS_LowerCell_BCorner_AP.Placement * AttachmentOffset * v5_6_Master#Local_CS097.Placement ^ -1
FEATURE [App::Link] LCFrame_Bracket_AS
  AssemblyType = Asm4EE
  AttachedBy = #Local_CS097
  AttachedTo = LowerCell#LCS_LowerCell_BCorner_AS
  AttachmentOffset = pos=(0,0,0) rot=(0,0,1;4.71239rad)
  LinkPlacement = pos=(-103,82,-65.2) rot=(0,0,-1;1.5708rad)
  LinkedObject = -> <external v5.6_Master.FCStd>#Body038
  Placement = pos=(-103,82,-65.2) rot=(0,0,-1;1.5708rad)
  expr: Placement = LowerCell.Placement * v5_6_Master#LCS_LowerCell_BCorner_AS.Placement * AttachmentOffset * v5_6_Master#Local_CS097.Placement ^ -1
FEATURE [App::Link] CollSpring_F
  AssemblyType = Asm4EE
  AttachedBy = #Local_CS191
  AttachedTo = LowerCell#LCS_LowerCell_CollPoint_F
  AttachmentOffset = pos=(0,0,11.6) rot=(0,0,1;0rad)
  LinkPlacement = pos=(-2.84e-14,-64,-53.6) rot=(0,0,1;0rad)
  LinkedObject = -> <external v5.6_Master.FCStd>#Body022010
  Placement = pos=(-2.84e-14,-64,-53.6) rot=(0,0,1;0rad)
  expr: Placement = LowerCell.Placement * v5_6_Master#LCS_LowerCell_CollPoint_F.Placement * AttachmentOffset * v5_6_Master#Local_CS191.Placement ^ -1
FEATURE [App::Link] CollSpring_AP
  AssemblyType = Asm4EE
  AttachedBy = #Local_CS191
  AttachedTo = LowerCell#LCS_LowerCell_CollPoint_AP
  AttachmentOffset = pos=(0,0,11.6) rot=(0,0,1;0rad)
  LinkPlacement = pos=(92,92,-53.6) rot=(0,0,1;0rad)
  LinkedObject = -> <external v5.6_Master.FCStd>#Body022010
  Placement = pos=(92,92,-53.6) rot=(0,0,1;0rad)
  expr: Placement = LowerCell.Placement * v5_6_Master#LCS_LowerCell_CollPoint_AP.Placement * AttachmentOffset * v5_6_Master#Local_CS191.Placement ^ -1
FEATURE [App::Link] CollSpring_AS
  AssemblyType = Asm4EE
  AttachedBy = #Local_CS191
  AttachedTo = LowerCell#LCS_LowerCell_CollPoint_AS
  AttachmentOffset = pos=(0,0,11.6) rot=(0,0,1;0rad)
  LinkPlacement = pos=(-92,92,-53.6) rot=(0,0,1;0rad)
  LinkedObject = -> <external v5.6_Master.FCStd>#Body022010
  Placement = pos=(-92,92,-53.6) rot=(0,0,1;0rad)
  expr: Placement = LowerCell.Placement * v5_6_Master#LCS_LowerCell_CollPoint_AS.Placement * AttachmentOffset * v5_6_Master#Local_CS191.Placement ^ -1
FEATURE [App::Link] MirrorClip_AP
  AssemblyType = Asm4EE
  AttachedBy = #Local_CS086
  AttachedTo = UpperCell#Local_CS081
  LinkPlacement = pos=(72.4784,72.4784,-31) rot=(0,0,-1;0.785398rad)
  LinkedObject = -> <external v5.6_Master.FCStd>#Body022
  Placement = pos=(72.4784,72.4784,-31) rot=(0,0,-1;0.785398rad)
  expr: Placement = UpperCell.Placement * v5_6_Master#Local_CS081.Placement * AttachmentOffset * v5_6_Master#Local_CS086.Placement ^ -1
FEATURE [App::Link] MirrorClip_FP
  AssemblyType = Asm4EE
  AttachedBy = #Local_CS086
  AttachedTo = UpperCell#Local_CS082
  LinkPlacement = pos=(72.4784,-72.4784,-31) rot=(0,0,-1;2.35619rad)
  LinkedObject = -> <external v5.6_Master.FCStd>#Body022
  Placement = pos=(72.4784,-72.4784,-31) rot=(0,0,-1;2.35619rad)
  expr: Placement = UpperCell.Placement * v5_6_Master#Local_CS082.Placement * AttachmentOffset * v5_6_Master#Local_CS086.Placement ^ -1
FEATURE [App::Link] MirrorClip_AS
  AssemblyType = Asm4EE
  AttachedBy = #Local_CS086
  AttachedTo = UpperCell#Local_CS080
  LinkPlacement = pos=(-72.4784,72.4784,-31) rot=(0,0,-1;5.49779rad)
  LinkedObject = -> <external v5.6_Master.FCStd>#Body022
  Placement = pos=(-72.4784,72.4784,-31) rot=(0,0,-1;5.49779rad)
  expr: Placement = UpperCell.Placement * v5_6_Master#Local_CS080.Placement * AttachmentOffset * v5_6_Master#Local_CS086.Placement ^ -1
FEATURE [App::Link] MirrorClip_FS
  AssemblyType = Asm4EE
  AttachedBy = #Local_CS086
  AttachedTo = UpperCell#Local_CS083
  LinkPlacement = pos=(-72.4784,-72.4784,-31) rot=(0,0,-1;3.92699rad)
  LinkedObject = -> <external v5.6_Master.FCStd>#Body022
  Placement = pos=(-72.4784,-72.4784,-31) rot=(0,0,-1;3.92699rad)
  expr: Placement = UpperCell.Placement * v5_6_Master#Local_CS083.Placement * AttachmentOffset * v5_6_Master#Local_CS086.Placement ^ -1
FEATURE [App::Link] Rocker_P_TNut_A
  AssemblyType = Asm4EE
  AttachedBy = #Local_CS100
  AttachedTo = Rocker_P#Local_CS024
  AttachmentOffset = pos=(0,0,0) rot=(0.707107,-0.707107,0;3.14159rad)
  LinkPlacement = pos=(121.8,113,-65.2) rot=(-0.57735,0.57735,-0.57735;2.0944rad)
  LinkedObject = -> <external v5.6_Master.FCStd>#Body039
  Placement = pos=(121.8,113,-65.2) rot=(-0.57735,0.57735,-0.57735;2.0944rad)
  expr: Placement = Rocker_P.Placement * v5_6_Master#Local_CS024.Placement * AttachmentOffset * v5_6_Master#Local_CS100.Placement ^ -1
FEATURE [App::Link] Rocker_P_TNut_F
  AssemblyType = Asm4EE
  AttachedBy = #Local_CS100
  AttachedTo = Rocker_P#Local_CS026
  AttachmentOffset = pos=(0,0,0) rot=(0.707107,-0.707107,0;3.14159rad)
  LinkPlacement = pos=(121.8,-113,-65.2) rot=(-0.57735,0.57735,-0.57735;2.0944rad)
  LinkedObject = -> <external v5.6_Master.FCStd>#Body039
  Placement = pos=(121.8,-113,-65.2) rot=(-0.57735,0.57735,-0.57735;2.0944rad)
  expr: Placement = Rocker_P.Placement * v5_6_Master#Local_CS026.Placement * AttachmentOffset * v5_6_Master#Local_CS100.Placement ^ -1
FEATURE [App::Link] Rocker_S_TNut_A
  AssemblyType = Asm4EE
  AttachedBy = #Local_CS100
  AttachedTo = Rocker_S#Local_CS028
  AttachmentOffset = pos=(0,0,0) rot=(0.707107,-0.707107,0;3.14159rad)
  LinkPlacement = pos=(-121.8,113,-65.2) rot=(0.57735,-0.57735,-0.57735;2.0944rad)
  LinkedObject = -> <external v5.6_Master.FCStd>#Body039
  Placement = pos=(-121.8,113,-65.2) rot=(0.57735,-0.57735,-0.57735;2.0944rad)
  expr: Placement = Rocker_S.Placement * v5_6_Master#Local_CS028.Placement * AttachmentOffset * v5_6_Master#Local_CS100.Placement ^ -1
FEATURE [App::Link] Rocker_S_TNut_F
  AssemblyType = Asm4EE
  AttachedBy = #Local_CS100
  AttachedTo = Rocker_S#Local_CS030
  AttachmentOffset = pos=(0,0,0) rot=(0.707107,-0.707107,0;3.14159rad)
  LinkPlacement = pos=(-121.8,-113,-65.2) rot=(0.57735,-0.57735,-0.57735;2.0944rad)
  LinkedObject = -> <external v5.6_Master.FCStd>#Body039
  Placement = pos=(-121.8,-113,-65.2) rot=(0.57735,-0.57735,-0.57735;2.0944rad)
  expr: Placement = Rocker_S.Placement * v5_6_Master#Local_CS030.Placement * AttachmentOffset * v5_6_Master#Local_CS100.Placement ^ -1
FEATURE [App::Link] LCBracket_AP_TNut_P
  AssemblyType = Asm4EE
  AttachedBy = #Local_CS100
  AttachedTo = LCFrame_Bracket_AP#Local_CS108
  LinkPlacement = pos=(104.2,64,-65.2) rot=(0.57735,0.57735,-0.57735;4.18879rad)
  LinkedObject = -> <external v5.6_Master.FCStd>#Body039
  Placement = pos=(104.2,64,-65.2) rot=(0.57735,0.57735,-0.57735;4.18879rad)
  expr: Placement = LCFrame_Bracket_AP.Placement * v5_6_Master#Local_CS108.Placement * AttachmentOffset * v5_6_Master#Local_CS100.Placement ^ -1
FEATURE [App::Link] LCBracket_AP_TNut_A
  AssemblyType = Asm4EE
  AttachedBy = #Local_CS100
  AttachedTo = LCFrame_Bracket_AP#Local_CS109
  LinkPlacement = pos=(85,83.2,-65.2) rot=(0,0.707107,-0.707107;3.14159rad)
  LinkedObject = -> <external v5.6_Master.FCStd>#Body039
  Placement = pos=(85,83.2,-65.2) rot=(0,0.707107,-0.707107;3.14159rad)
  expr: Placement = LCFrame_Bracket_AP.Placement * v5_6_Master#Local_CS109.Placement * AttachmentOffset * v5_6_Master#Local_CS100.Placement ^ -1
FEATURE [App::Link] LCBracket_AS_TNut_S
  AssemblyType = Asm4EE
  AttachedBy = #Local_CS100
  AttachedTo = LCFrame_Bracket_AS#Local_CS109
  LinkPlacement = pos=(-104.2,64,-65.2) rot=(-0.57735,0.57735,-0.57735;2.0944rad)
  LinkedObject = -> <external v5.6_Master.FCStd>#Body039
  Placement = pos=(-104.2,64,-65.2) rot=(-0.57735,0.57735,-0.57735;2.0944rad)
  expr: Placement = LCFrame_Bracket_AS.Placement * v5_6_Master#Local_CS109.Placement * AttachmentOffset * v5_6_Master#Local_CS100.Placement ^ -1
FEATURE [App::Link] LCBracket_AS_TNut_A
  AssemblyType = Asm4EE
  AttachedBy = #Local_CS100
  AttachedTo = LCFrame_Bracket_AS#Local_CS108
  LinkPlacement = pos=(-85,83.2,-65.2) rot=(0,0.707107,-0.707107;3.14159rad)
  LinkedObject = -> <external v5.6_Master.FCStd>#Body039
  Placement = pos=(-85,83.2,-65.2) rot=(0,0.707107,-0.707107;3.14159rad)
  expr: Placement = LCFrame_Bracket_AS.Placement * v5_6_Master#Local_CS108.Placement * AttachmentOffset * v5_6_Master#Local_CS100.Placement ^ -1
FEATURE [Part::FeaturePython] Screw  label="M6x50-Screw"  # Fasteners workbench fastener (typed FeaturePython)
  AssemblyType = Asm4EE
  AttachedBy = Origin
  AttachedTo = UpperCell#Local_CS009
  Placement = pos=(0,-64,-33) rot=(0,0,1;0rad)
  diameter = 4
  invert = false
  length = 10
  lengthCustom = 50
  matchOuter = false
  offset = 0
  thread = false
  type = 38
  expr: Placement = UpperCell.Placement * v5_6_Master#Local_CS009.Placement * AttachmentOffset
FEATURE [Part::FeaturePython] Screw001  label="M6x60-Screw"  # Fasteners workbench fastener (typed FeaturePython)
  AssemblyType = Asm4EE
  AttachedBy = Origin
  AttachedTo = LowerCell#LCS_LowerCell_CollPoint_AP
  AttachmentOffset = pos=(0,0,-11.6) rot=(1,0,0;3.14159rad)
  Placement = pos=(92,92,-76.8) rot=(-1,0,0;3.14159rad)
  diameter = 8
  invert = false
  length = 11
  lengthCustom = 60
  matchOuter = false
  offset = 0
  thread = false
  type = 27
  expr: Placement = LowerCell.Placement * v5_6_Master#LCS_LowerCell_CollPoint_AP.Placement * AttachmentOffset
FEATURE [Part::FeaturePython] Screw002  label="M6x60-Screw001"  # Fasteners workbench fastener (typed FeaturePython)
  AssemblyType = Asm4EE
  AttachedBy = Origin
  AttachedTo = LowerCell#LCS_LowerCell_CollPoint_AS
  AttachmentOffset = pos=(0,0,-11.6) rot=(1,0,0;3.14159rad)
  Placement = pos=(-92,92,-76.8) rot=(-1,0,0;3.14159rad)
  diameter = 8
  invert = false
  length = 11
  lengthCustom = 60
  matchOuter = false
  offset = 0
  thread = false
  type = 27
  expr: Placement = LowerCell.Placement * v5_6_Master#LCS_LowerCell_CollPoint_AS.Placement * AttachmentOffset
FEATURE [Part::FeaturePython] Washer  label="M6-Washer"  # Fasteners workbench fastener (typed FeaturePython)
  AssemblyType = Asm4EE
  AttachedBy = Origin
  AttachedTo = LowerCell#LCS_LowerCell_CollPoint_F
  AttachmentOffset = pos=(0,0,10) rot=(0,0,1;0rad)
  Placement = pos=(-2.84e-14,-64,-55.2) rot=(0,0,1;0rad)
  diameter = 5
  invert = false
  matchOuter = false
  offset = 0
  type = 6
  expr: Placement = LowerCell.Placement * v5_6_Master#LCS_LowerCell_CollPoint_F.Placement * AttachmentOffset
FEATURE [Part::FeaturePython] Washer001  label="M6-Washer413"  # Fasteners workbench fastener (typed FeaturePython)
  AssemblyType = Asm4EE
  AttachedBy = Origin
  AttachedTo = LowerCell#LCS_LowerCell_CollPoint_F
  AttachmentOffset = pos=(0,0,26.6) rot=(0,0,1;0rad)
  Placement = pos=(-2.84e-14,-64,-38.6) rot=(0,0,1;0rad)
  diameter = 5
  invert = false
  matchOuter = false
  offset = 0
  type = 6
  expr: Placement = LowerCell.Placement * v5_6_Master#LCS_LowerCell_CollPoint_F.Placement * AttachmentOffset
FEATURE [Part::FeaturePython] Washer002  label="M6-Washer414"  # Fasteners workbench fastener (typed FeaturePython)
  AssemblyType = Asm4EE
  AttachedBy = Origin
  AttachedTo = LowerCell#LCS_LowerCell_CollPoint_AP
  AttachmentOffset = pos=(0,0,10) rot=(0,0,1;0rad)
  Placement = pos=(92,92,-55.2) rot=(0,0,1;0rad)
  diameter = 5
  invert = false
  matchOuter = false
  offset = 0
  type = 6
  expr: Placement = LowerCell.Placement * v5_6_Master#LCS_LowerCell_CollPoint_AP.Placement * AttachmentOffset
FEATURE [Part::FeaturePython] Washer003  label="M6-Washer415"  # Fasteners workbench fastener (typed FeaturePython)
  AssemblyType = Asm4EE
  AttachedBy = Origin
  AttachedTo = LowerCell#LCS_LowerCell_CollPoint_AP
  AttachmentOffset = pos=(0,0,26.6) rot=(0,0,1;0rad)
  Placement = pos=(92,92,-38.6) rot=(0,0,1;0rad)
  diameter = 5
  invert = false
  matchOuter = false
  offset = 0
  type = 6
  expr: Placement = LowerCell.Placement * v5_6_Master#LCS_LowerCell_CollPoint_AP.Placement * AttachmentOffset
FEATURE [Part::FeaturePython] Washer004  label="M6-Washer416"  # Fasteners workbench fastener (typed FeaturePython)
  AssemblyType = Asm4EE
  AttachedBy = Origin
  AttachedTo = LowerCell#LCS_LowerCell_CollPoint_AS
  AttachmentOffset = pos=(0,0,10) rot=(0,0,1;0rad)
  Placement = pos=(-92,92,-55.2) rot=(0,0,1;0rad)
  diameter = 5
  invert = false
  matchOuter = false
  offset = 0
  type = 6
  expr: Placement = LowerCell.Placement * v5_6_Master#LCS_LowerCell_CollPoint_AS.Placement * AttachmentOffset
FEATURE [Part::FeaturePython] Washer005  label="M6-Washer417"  # Fasteners workbench fastener (typed FeaturePython)
  AssemblyType = Asm4EE
  AttachedBy = Origin
  AttachedTo = LowerCell#LCS_LowerCell_CollPoint_AS
  AttachmentOffset = pos=(0,0,26.6) rot=(0,0,1;0rad)
  Placement = pos=(-92,92,-38.6) rot=(0,0,1;0rad)
  diameter = 5
  invert = false
  matchOuter = false
  offset = 0
  type = 6
  expr: Placement = LowerCell.Placement * v5_6_Master#LCS_LowerCell_CollPoint_AS.Placement * AttachmentOffset
FEATURE [Part::FeaturePython] Screw003  label="M4x35-Screw"  # Fasteners workbench fastener (typed FeaturePython)
  AssemblyType = Asm4EE
  AttachedBy = Origin
  AttachedTo = UpperCell#Local_CS114
  Placement = pos=(-81.6708,-71.0642,-37) rot=(0.382683,0.92388,0;3.14159rad)
  diameter = 5
  invert = false
  length = 9
  lengthCustom = 35
  matchOuter = false
  offset = 0
  thread = false
  type = 32
  expr: Placement = UpperCell.Placement * v5_6_Master#Local_CS114.Placement * AttachmentOffset
FEATURE [Part::FeaturePython] Screw004  label="M4x35-Screw211"  # Fasteners workbench fastener (typed FeaturePython)
  AssemblyType = Asm4EE
  AttachedBy = Origin
  AttachedTo = UpperCell#Local_CS115
  Placement = pos=(-71.0642,-81.6708,-37) rot=(0.382683,0.92388,0;3.14159rad)
  diameter = 5
  invert = false
  length = 9
  lengthCustom = 35
  matchOuter = false
  offset = 0
  thread = false
  type = 32
  expr: Placement = UpperCell.Placement * v5_6_Master#Local_CS115.Placement * AttachmentOffset
FEATURE [Part::FeaturePython] Screw005  label="M4x35-Screw212"  # Fasteners workbench fastener (typed FeaturePython)
  AssemblyType = Asm4EE
  AttachedBy = Origin
  AttachedTo = UpperCell#Local_CS116
  Placement = pos=(71.0642,-81.6708,-37) rot=(-0.382683,0.92388,0;3.14159rad)
  diameter = 5
  invert = false
  length = 9
  lengthCustom = 35
  matchOuter = false
  offset = 0
  thread = false
  type = 32
  expr: Placement = UpperCell.Placement * v5_6_Master#Local_CS116.Placement * AttachmentOffset
FEATURE [Part::FeaturePython] Screw006  label="M4x35-Screw213"  # Fasteners workbench fastener (typed FeaturePython)
  AssemblyType = Asm4EE
  AttachedBy = Origin
  AttachedTo = UpperCell#Local_CS117
  Placement = pos=(81.6708,-71.0642,-37) rot=(-0.382683,0.92388,0;3.14159rad)
  diameter = 5
  invert = false
  length = 9
  lengthCustom = 35
  matchOuter = false
  offset = 0
  thread = false
  type = 32
  expr: Placement = UpperCell.Placement * v5_6_Master#Local_CS117.Placement * AttachmentOffset
FEATURE [Part::FeaturePython] Screw007  label="M4x35-Screw214"  # Fasteners workbench fastener (typed FeaturePython)
  AssemblyType = Asm4EE
  AttachedBy = Origin
  AttachedTo = UpperCell#Local_CS118
  Placement = pos=(-81.6708,71.0642,-37) rot=(0.92388,0.382683,0;3.14159rad)
  diameter = 5
  invert = false
  length = 9
  lengthCustom = 35
  matchOuter = false
  offset = 0
  thread = false
  type = 32
  expr: Placement = UpperCell.Placement * v5_6_Master#Local_CS118.Placement * AttachmentOffset
FEATURE [Part::FeaturePython] Screw008  label="M4x35-Screw215"  # Fasteners workbench fastener (typed FeaturePython)
  AssemblyType = Asm4EE
  AttachedBy = Origin
  AttachedTo = UpperCell#Local_CS119
  Placement = pos=(-71.0642,81.6708,-37) rot=(0.92388,0.382683,0;3.14159rad)
  diameter = 5
  invert = false
  length = 9
  lengthCustom = 35
  matchOuter = false
  offset = 0
  thread = false
  type = 32
  expr: Placement = UpperCell.Placement * v5_6_Master#Local_CS119.Placement * AttachmentOffset
FEATURE [Part::FeaturePython] Screw009  label="M4x35-Screw216"  # Fasteners workbench fastener (typed FeaturePython)
  AssemblyType = Asm4EE
  AttachedBy = Origin
  AttachedTo = UpperCell#Local_CS120
  Placement = pos=(81.6708,71.0642,-37) rot=(0.92388,-0.382683,0;3.14159rad)
  diameter = 5
  invert = false
  length = 9
  lengthCustom = 35
  matchOuter = false
  offset = 0
  thread = false
  type = 32
  expr: Placement = UpperCell.Placement * v5_6_Master#Local_CS120.Placement * AttachmentOffset
FEATURE [Part::FeaturePython] Screw010  label="M4x35-Screw217"  # Fasteners workbench fastener (typed FeaturePython)
  AssemblyType = Asm4EE
  AttachedBy = Origin
  AttachedTo = UpperCell#Local_CS121
  Placement = pos=(71.0642,81.6708,-37) rot=(0.92388,-0.382683,0;3.14159rad)
  diameter = 5
  invert = false
  length = 9
  lengthCustom = 35
  matchOuter = false
  offset = 0
  thread = false
  type = 32
  expr: Placement = UpperCell.Placement * v5_6_Master#Local_CS121.Placement * AttachmentOffset
FEATURE [Part::FeaturePython] Screw011  label="M5x10-Screw"  # Fasteners workbench fastener (typed FeaturePython)
  AssemblyType = Asm4EE
  AttachedBy = Origin
  AttachedTo = LCFrame_Bracket_AP#Local_CS098
  Placement = pos=(98.5,64,-65.2) rot=(0.57735,-0.57735,-0.57735;2.0944rad)
  diameter = 6
  invert = false
  length = 1
  lengthCustom = 10
  matchOuter = false
  offset = 0
  thread = false
  type = 32
  expr: Placement = LCFrame_Bracket_AP.Placement * v5_6_Master#Local_CS098.Placement * AttachmentOffset
FEATURE [Part::FeaturePython] Screw012  label="M5x10-Screw133"  # Fasteners workbench fastener (typed FeaturePython)
  AssemblyType = Asm4EE
  AttachedBy = Origin
  AttachedTo = LCFrame_Bracket_AP#Local_CS099
  Placement = pos=(85,77.5,-65.2) rot=(0.57735,0.57735,-0.57735;2.0944rad)
  diameter = 6
  invert = false
  length = 1
  lengthCustom = 10
  matchOuter = false
  offset = 0
  thread = false
  type = 32
  expr: Placement = LCFrame_Bracket_AP.Placement * v5_6_Master#Local_CS099.Placement * AttachmentOffset
FEATURE [Part::FeaturePython] Screw013  label="M5x10-Screw134"  # Fasteners workbench fastener (typed FeaturePython)
  AssemblyType = Asm4EE
  AttachedBy = Origin
  AttachedTo = LCFrame_Bracket_AS#Local_CS098
  Placement = pos=(-85,77.5,-65.2) rot=(1,0,0;1.5708rad)
  diameter = 6
  invert = false
  length = 1
  lengthCustom = 10
  matchOuter = false
  offset = 0
  thread = false
  type = 32
  expr: Placement = LCFrame_Bracket_AS.Placement * v5_6_Master#Local_CS098.Placement * AttachmentOffset
FEATURE [Part::FeaturePython] Screw014  label="M5x10-Screw135"  # Fasteners workbench fastener (typed FeaturePython)
  AssemblyType = Asm4EE
  AttachedBy = Origin
  AttachedTo = LCFrame_Bracket_AS#Local_CS099
  Placement = pos=(-98.5,64,-65.2) rot=(0,1,0;1.5708rad)
  diameter = 6
  invert = false
  length = 1
  lengthCustom = 10
  matchOuter = false
  offset = 0
  thread = false
  type = 32
  expr: Placement = LCFrame_Bracket_AS.Placement * v5_6_Master#Local_CS099.Placement * AttachmentOffset
FEATURE [App::Link] PoleBase_TNut_A
  AssemblyType = Asm4EE
  AttachedBy = #Local_CS100
  AttachedTo = LowerCell#LCS_LowerCell_Pole_AP
  AttachmentOffset = pos=(0,0,0) rot=(0,0,1;1.5708rad)
  LinkPlacement = pos=(113,113,-56.4) rot=(0,0,1;4.71239rad)
  LinkedObject = -> <external v5.6_Master.FCStd>#Body039
  Placement = pos=(113,113,-56.4) rot=(0,0,1;4.71239rad)
  expr: Placement = LowerCell.Placement * v5_6_Master#LCS_LowerCell_Pole_AP.Placement * AttachmentOffset * v5_6_Master#Local_CS100.Placement ^ -1
FEATURE [App::Link] PoleBase_TNut_F
  AssemblyType = Asm4EE
  AttachedBy = #Local_CS100
  AttachedTo = LowerCell#LCS_LowerCell_Pole_FP
  AttachmentOffset = pos=(0,0,0) rot=(0,0,1;1.5708rad)
  LinkPlacement = pos=(113,-113,-56.4) rot=(0,0,1;4.71239rad)
  LinkedObject = -> <external v5.6_Master.FCStd>#Body039
  Placement = pos=(113,-113,-56.4) rot=(0,0,1;4.71239rad)
  expr: Placement = LowerCell.Placement * v5_6_Master#LCS_LowerCell_Pole_FP.Placement * AttachmentOffset * v5_6_Master#Local_CS100.Placement ^ -1
FEATURE [PartDesign::CoordinateSystem] LCS_Pivot
  AttacherType = Attacher::AttachEngine3D
  Placement = pos=(0,0,79.8) rot=(0,0,1;0rad)
  expr: Placement = LowerCell.Placement * v5_6_Master#LCS_LowerCell_Pivot_X.Placement * AttachmentOffset
FEATURE [PartDesign::CoordinateSystem] LCS_SecondaryAssembly
  AttacherType = Attacher::AttachEngine3D
  Placement = pos=(0,0,834) rot=(0,0,1;0rad)
  expr: Placement = PrimaryMirror.Placement * v5_6_Master#Local_CS039.Placement * AttachmentOffset
FEATURE [PartDesign::CoordinateSystem] LCS_Primary_Pole_AP
  AttacherType = Attacher::AttachEngine3D
  Placement = pos=(113,113,-55.2) rot=(0,0,1;0rad)
  expr: Placement = LowerCell.Placement * v5_6_Master#LCS_LowerCell_Pole_AP.Placement * AttachmentOffset
FEATURE [PartDesign::CoordinateSystem] LCS_Primary_Pole_AS
  AttacherType = Attacher::AttachEngine3D
  Placement = pos=(-113,113,-65.2) rot=(0,0,1;0rad)
  expr: Placement = LowerCell.Placement * v5_6_Master#LCS_LowerCell_Pole_AS.Placement * AttachmentOffset
FEATURE [PartDesign::CoordinateSystem] LCS_Primary_Pole_FP
  AttacherType = Attacher::AttachEngine3D
  Placement = pos=(113,-113,-55.2) rot=(0,0,1;0rad)
  expr: Placement = LowerCell.Placement * v5_6_Master#LCS_LowerCell_Pole_FP.Placement * AttachmentOffset
FEATURE [PartDesign::CoordinateSystem] LCS_Primary_Pole_FS
  AttacherType = Attacher::AttachEngine3D
  Placement = pos=(-113,-113,-55.2) rot=(0,0,1;0rad)
  expr: Placement = LowerCell.Placement * v5_6_Master#LCS_LowerCell_Pole_FS.Placement * AttachmentOffset
FEATURE [Part::FeaturePython] Washer006  label="M6-Washer418"  # Fasteners workbench fastener (typed FeaturePython)
  AssemblyType = Asm4EE
  AttachedBy = Origin
  AttachedTo = LowerCell#LCS_LowerCell_CollPoint_F
  AttachmentOffset = pos=(0,0,-10) rot=(1,0,0;3.14159rad)
  Placement = pos=(-2.84e-14,-64,-75.2) rot=(-1,0,0;3.14159rad)
  diameter = 7
  invert = false
  matchOuter = false
  offset = 0
  type = 3
  expr: Placement = LowerCell.Placement * v5_6_Master#LCS_LowerCell_CollPoint_F.Placement * AttachmentOffset
FEATURE [Part::FeaturePython] Nut  label="M6-Nut"  # Fasteners workbench fastener (typed FeaturePython)
  AssemblyType = Asm4EE
  AttachedBy = Origin
  AttachedTo = LowerCell#LCS_LowerCell_CollPoint_F
  AttachmentOffset = pos=(0,0,-11.8) rot=(1,0,0;3.14159rad)
  Placement = pos=(-2.84e-14,-64,-77) rot=(-1,0,0;3.14159rad)
  diameter = 8
  invert = false
  matchOuter = false
  offset = 0
  thread = false
  type = 7
  expr: Placement = LowerCell.Placement * v5_6_Master#LCS_LowerCell_CollPoint_F.Placement * AttachmentOffset
FEATURE [Part::FeaturePython] Washer007  label="M6-Washer419"  # Fasteners workbench fastener (typed FeaturePython)
  AssemblyType = Asm4EE
  AttachedBy = Origin
  AttachedTo = UpperCell#Local_CS011
  Placement = pos=(92,92,-31) rot=(0,0,1;0rad)
  diameter = 5
  invert = false
  matchOuter = false
  offset = 0
  type = 6
  expr: Placement = UpperCell.Placement * v5_6_Master#Local_CS011.Placement * AttachmentOffset
FEATURE [Part::FeaturePython] Washer008  label="M6-Washer420"  # Fasteners workbench fastener (typed FeaturePython)
  AssemblyType = Asm4EE
  AttachedBy = Origin
  AttachedTo = UpperCell#Local_CS010
  Placement = pos=(-92,92,-31) rot=(0,0,1;0rad)
  diameter = 5
  invert = false
  matchOuter = false
  offset = 0
  type = 6
  expr: Placement = UpperCell.Placement * v5_6_Master#Local_CS010.Placement * AttachmentOffset
FEATURE [Part::FeaturePython] Washer009  label="M6-Washer421"  # Fasteners workbench fastener (typed FeaturePython)
  AssemblyType = Asm4EE
  AttachedBy = Origin
  AttachedTo = LowerCell#LCS_LowerCell_CollPoint_AP
  AttachmentOffset = pos=(0,0,-10) rot=(1,0,0;3.14159rad)
  Placement = pos=(92,92,-75.2) rot=(-1,0,0;3.14159rad)
  diameter = 7
  invert = false
  matchOuter = false
  offset = 0
  type = 3
  expr: Placement = LowerCell.Placement * v5_6_Master#LCS_LowerCell_CollPoint_AP.Placement * AttachmentOffset
FEATURE [Part::FeaturePython] Washer010  label="M6-Washer422"  # Fasteners workbench fastener (typed FeaturePython)
  AssemblyType = Asm4EE
  AttachedBy = Origin
  AttachedTo = LowerCell#LCS_LowerCell_CollPoint_AS
  AttachmentOffset = pos=(0,0,-10) rot=(1,0,0;3.14159rad)
  Placement = pos=(-92,92,-75.2) rot=(-1,0,0;3.14159rad)
  diameter = 7
  invert = false
  matchOuter = false
  offset = 0
  type = 3
  expr: Placement = LowerCell.Placement * v5_6_Master#LCS_LowerCell_CollPoint_AS.Placement * AttachmentOffset
FEATURE [App::Link] CounterWeightClamp
  AssemblyType = Asm4EE
  AttachedBy = #Local_CS209
  AttachedTo = LowerCell#LCS_LowerCell_Counterweight
  AttachmentOffset = pos=(0,0,0) rot=(1,0,0;3.14159rad)
  LinkPlacement = pos=(4.09e-14,92,-75.2) rot=(0,0,1;0rad)
  LinkedObject = -> <external v5.6_Master.FCStd>#Body022019
  Placement = pos=(4.09e-14,92,-75.2) rot=(0,0,1;0rad)
  expr: Placement = LowerCell.Placement * v5_6_Master#LCS_LowerCell_Counterweight.Placement * AttachmentOffset * v5_6_Master#Local_CS209.Placement ^ -1
FEATURE [App::Link] CW_TNut
  AssemblyType = Asm4EE
  AttachedBy = #Local_CS100
  AttachedTo = CounterWeightClamp#Local_CS209
  LinkPlacement = pos=(4.09e-14,92,-74) rot=(0,-1,0;3.14159rad)
  LinkedObject = -> <external v5.6_Master.FCStd>#Body039
  Placement = pos=(4.09e-14,92,-74) rot=(0,-1,0;3.14159rad)
  expr: Placement = CounterWeightClamp.Placement * v5_6_Master#Local_CS209.Placement * AttachmentOffset * v5_6_Master#Local_CS100.Placement ^ -1
FEATURE [Part::FeaturePython] Screw026  label="M5x20-Screw"  # Fasteners workbench fastener (typed FeaturePython)
  AssemblyType = Asm4EE
  AttachedBy = Origin
  AttachedTo = CounterWeightClamp#Local_CS210
  AttachmentOffset = pos=(0,0,0) rot=(1,0,0;3.14159rad)
  Placement = pos=(4.75e-14,92,-85.2) rot=(0,-1,0;3.14159rad)
  diameter = 7
  invert = false
  length = 5
  lengthCustom = 20
  matchOuter = false
  offset = 0
  thread = false
  type = 27
  expr: Placement = CounterWeightClamp.Placement * v5_6_Master#Local_CS210.Placement * AttachmentOffset
FEATURE [App::Link] CounterWeight
  AssemblyType = Asm4EE
  AttachedBy = #Local_CS218
  AttachedTo = CounterWeightClamp#Local_CS211
  LinkPlacement = pos=(4.09e-14,92,-95.2) rot=(0,0,-1;4.71239rad)
  LinkedObject = -> <external v5.6_Master.FCStd>#Body017
  Placement = pos=(4.09e-14,92,-95.2) rot=(0,0,-1;4.71239rad)
  expr: Placement = CounterWeightClamp.Placement * v5_6_Master#Local_CS211.Placement * AttachmentOffset * v5_6_Master#Local_CS218.Placement ^ -1
FEATURE [Part::FeaturePython] Nut001  label="M4-Nut"  # Fasteners workbench fastener (typed FeaturePython)
  AssemblyType = Asm4EE
  AttachedBy = Origin
  AttachedTo = MirrorClip_AP#Local_CS087
  AttachmentOffset = pos=(0,0,24) rot=(0,0,1;1.5708rad)
  Placement = pos=(81.3173,70.7107,-7) rot=(0,0,1;2.35619rad)
  diameter = 6
  invert = false
  matchOuter = false
  offset = 0
  thread = false
  type = 7
  expr: Placement = MirrorClip_AP.Placement * v5_6_Master#Local_CS087.Placement * AttachmentOffset
FEATURE [Part::FeaturePython] Nut002  label="M4-Nut079"  # Fasteners workbench fastener (typed FeaturePython)
  AssemblyType = Asm4EE
  AttachedBy = Origin
  AttachedTo = MirrorClip_AP#Local_CS088
  AttachmentOffset = pos=(0,0,24) rot=(0,0,1;1.5708rad)
  Placement = pos=(70.7107,81.3173,-7) rot=(0,0,1;2.35619rad)
  diameter = 6
  invert = false
  matchOuter = false
  offset = 0
  thread = false
  type = 7
  expr: Placement = MirrorClip_AP.Placement * v5_6_Master#Local_CS088.Placement * AttachmentOffset
FEATURE [Part::FeaturePython] Nut003  label="M4-Nut080"  # Fasteners workbench fastener (typed FeaturePython)
  AssemblyType = Asm4EE
  AttachedBy = Origin
  AttachedTo = MirrorClip_FP#Local_CS087
  AttachmentOffset = pos=(0,0,24) rot=(0,0,1;1.5708rad)
  Placement = pos=(70.7107,-81.3173,-7) rot=(0,0,1;0.785398rad)
  diameter = 6
  invert = false
  matchOuter = false
  offset = 0
  thread = false
  type = 7
  expr: Placement = MirrorClip_FP.Placement * v5_6_Master#Local_CS087.Placement * AttachmentOffset
FEATURE [Part::FeaturePython] Nut004  label="M4-Nut081"  # Fasteners workbench fastener (typed FeaturePython)
  AssemblyType = Asm4EE
  AttachedBy = Origin
  AttachedTo = MirrorClip_FP#Local_CS088
  AttachmentOffset = pos=(0,0,24) rot=(0,0,1;1.5708rad)
  Placement = pos=(81.3173,-70.7107,-7) rot=(0,0,1;0.785398rad)
  diameter = 6
  invert = false
  matchOuter = false
  offset = 0
  thread = false
  type = 7
  expr: Placement = MirrorClip_FP.Placement * v5_6_Master#Local_CS088.Placement * AttachmentOffset
FEATURE [Part::FeaturePython] Nut005  label="M4-Nut082"  # Fasteners workbench fastener (typed FeaturePython)
  AssemblyType = Asm4EE
  AttachedBy = Origin
  AttachedTo = MirrorClip_AS#Local_CS087
  AttachmentOffset = pos=(0,0,24) rot=(0,0,1;1.5708rad)
  Placement = pos=(-70.7107,81.3173,-7) rot=(0,0,-1;2.35619rad)
  diameter = 6
  invert = false
  matchOuter = false
  offset = 0
  thread = false
  type = 7
  expr: Placement = MirrorClip_AS.Placement * v5_6_Master#Local_CS087.Placement * AttachmentOffset
FEATURE [Part::FeaturePython] Nut006  label="M4-Nut083"  # Fasteners workbench fastener (typed FeaturePython)
  AssemblyType = Asm4EE
  AttachedBy = Origin
  AttachedTo = MirrorClip_AS#Local_CS088
  AttachmentOffset = pos=(0,0,24) rot=(0,0,1;0rad)
  Placement = pos=(-81.3173,70.7107,-7) rot=(0,0,-1;3.92699rad)
  diameter = 6
  invert = false
  matchOuter = false
  offset = 0
  thread = false
  type = 7
  expr: Placement = MirrorClip_AS.Placement * v5_6_Master#Local_CS088.Placement * AttachmentOffset
FEATURE [Part::FeaturePython] Nut007  label="M4-Nut084"  # Fasteners workbench fastener (typed FeaturePython)
  AssemblyType = Asm4EE
  AttachedBy = Origin
  AttachedTo = MirrorClip_FS#Local_CS087
  AttachmentOffset = pos=(0,0,24) rot=(0,0,1;1.5708rad)
  Placement = pos=(-81.3173,-70.7107,-7) rot=(0,0,-1;0.785398rad)
  diameter = 6
  invert = false
  matchOuter = false
  offset = 0
  thread = false
  type = 7
  expr: Placement = MirrorClip_FS.Placement * v5_6_Master#Local_CS087.Placement * AttachmentOffset
FEATURE [Part::FeaturePython] Nut008  label="M4-Nut085"  # Fasteners workbench fastener (typed FeaturePython)
  AssemblyType = Asm4EE
  AttachedBy = Origin
  AttachedTo = MirrorClip_FS#Local_CS088
  AttachmentOffset = pos=(0,0,24) rot=(0,0,1;1.5708rad)
  Placement = pos=(-70.7107,-81.3173,-7) rot=(0,0,-1;0.785398rad)
  diameter = 6
  invert = false
  matchOuter = false
  offset = 0
  thread = false
  type = 7
  expr: Placement = MirrorClip_FS.Placement * v5_6_Master#Local_CS088.Placement * AttachmentOffset
FEATURE [App::Link] RockerKnob_AP
  AssemblyType = Asm4EE
  AttachedBy = #Local_CS235
  AttachedTo = Rocker_P#Local_CS028
  LinkPlacement = pos=(133,113,-65.2) rot=(-0.57735,-0.57735,-0.57735;4.18879rad)
  LinkedObject = -> <external v5.6_Master.FCStd>#Body022032
  Placement = pos=(133,113,-65.2) rot=(-0.57735,-0.57735,-0.57735;4.18879rad)
  expr: Placement = Rocker_P.Placement * v5_6_Master#Local_CS028.Placement * AttachmentOffset * v5_6_Master#Local_CS235.Placement ^ -1
FEATURE [App::Link] RockerKnob_FP
  AssemblyType = Asm4EE
  AttachedBy = #Local_CS235
  AttachedTo = Rocker_P#Local_CS030
  LinkPlacement = pos=(133,-113,-65.2) rot=(-0.57735,-0.57735,-0.57735;4.18879rad)
  LinkedObject = -> <external v5.6_Master.FCStd>#Body022032
  Placement = pos=(133,-113,-65.2) rot=(-0.57735,-0.57735,-0.57735;4.18879rad)
  expr: Placement = Rocker_P.Placement * v5_6_Master#Local_CS030.Placement * AttachmentOffset * v5_6_Master#Local_CS235.Placement ^ -1
FEATURE [App::Link] RockerKnob_AS
  AssemblyType = Asm4EE
  AttachedBy = #Local_CS235
  AttachedTo = Rocker_S#Local_CS024
  LinkPlacement = pos=(-133,113,-65.2) rot=(-0.57735,-0.57735,0.57735;2.0944rad)
  LinkedObject = -> <external v5.6_Master.FCStd>#Body022032
  Placement = pos=(-133,113,-65.2) rot=(-0.57735,-0.57735,0.57735;2.0944rad)
  expr: Placement = Rocker_S.Placement * v5_6_Master#Local_CS024.Placement * AttachmentOffset * v5_6_Master#Local_CS235.Placement ^ -1
FEATURE [App::Link] RockerKnob_FS
  AssemblyType = Asm4EE
  AttachedBy = #Local_CS235
  AttachedTo = Rocker_S#Local_CS026
  LinkPlacement = pos=(-133,-113,-65.2) rot=(-0.57735,-0.57735,0.57735;2.0944rad)
  LinkedObject = -> <external v5.6_Master.FCStd>#Body022032
  Placement = pos=(-133,-113,-65.2) rot=(-0.57735,-0.57735,0.57735;2.0944rad)
  expr: Placement = Rocker_S.Placement * v5_6_Master#Local_CS026.Placement * AttachmentOffset * v5_6_Master#Local_CS235.Placement ^ -1
FEATURE [App::Link] CollKnob_AP001  label="CollKnob_AP"
  AssemblyType = Asm4EE
  AttachedBy = #Local_CS234
  AttachedTo = UpperCell#Local_CS011
  AttachmentOffset = pos=(0,0,1.6) rot=(0,0,1;0rad)
  LinkPlacement = pos=(92,92,-29.4) rot=(0,0,-1;1.5708rad)
  LinkedObject = -> <external v5.6_Master.FCStd>#Body022030
  Placement = pos=(92,92,-29.4) rot=(0,0,-1;1.5708rad)
  expr: Placement = UpperCell.Placement * v5_6_Master#Local_CS011.Placement * AttachmentOffset * v5_6_Master#Local_CS234.Placement ^ -1
FEATURE [App::Link] CollKnob_AS001  label="CollKnob_AS"
  AssemblyType = Asm4EE
  AttachedBy = #Local_CS234
  AttachedTo = UpperCell#Local_CS010
  AttachmentOffset = pos=(0,0,1.6) rot=(0,0,1;0rad)
  LinkPlacement = pos=(-92,92,-29.4) rot=(0,0,-1;1.5708rad)
  LinkedObject = -> <external v5.6_Master.FCStd>#Body022030
  Placement = pos=(-92,92,-29.4) rot=(0,0,-1;1.5708rad)
  expr: Placement = UpperCell.Placement * v5_6_Master#Local_CS010.Placement * AttachmentOffset * v5_6_Master#Local_CS234.Placement ^ -1
FEATURE [App::Link] PoleBase_TNut_AS
  AssemblyType = Asm4EE
  AttachedBy = #Local_CS100
  AttachedTo = LowerCell#LCS_LowerCell_Pole_AS
  AttachmentOffset = pos=(0,0,10) rot=(0,0,1;1.5708rad)
  LinkPlacement = pos=(-113,113,-56.4) rot=(0,0,1;4.71239rad)
  LinkedObject = -> <external v5.6_Master.FCStd>#Body039
  Placement = pos=(-113,113,-56.4) rot=(0,0,1;4.71239rad)
  expr: Placement = LowerCell.Placement * v5_6_Master#LCS_LowerCell_Pole_AS.Placement * AttachmentOffset * v5_6_Master#Local_CS100.Placement ^ -1
FEATURE [App::Link] PoleBase_TNut_FS
  AssemblyType = Asm4EE
  AttachedBy = #Local_CS100
  AttachedTo = LowerCell#LCS_LowerCell_Pole_FS
  AttachmentOffset = pos=(0,0,0) rot=(0,0,1;1.5708rad)
  LinkPlacement = pos=(-113,-113,-56.4) rot=(0,0,1;4.71239rad)
  LinkedObject = -> <external v5.6_Master.FCStd>#Body039
  Placement = pos=(-113,-113,-56.4) rot=(0,0,1;4.71239rad)
  expr: Placement = LowerCell.Placement * v5_6_Master#LCS_LowerCell_Pole_FS.Placement * AttachmentOffset * v5_6_Master#Local_CS100.Placement ^ -1
FEATURE [App::Part] Model  label="Primary"
  Configuration = 0
  Group = -> [LCS_Origin,Constraints,Variables,PrimaryMirror,UpperCell,LowerPad_A,LowerPad_FP,LowerPad_FS,LowerCell,Rocker_P,Rocker_S,LCFrame_Bracket_AP,LCFrame_Bracket_AS,CollSpring_F,CollSpring_AP,CollSpring_AS,MirrorClip_AP,MirrorClip_FP,MirrorClip_AS,MirrorClip_FS,Rocker_P_TNut_A,Rocker_P_TNut_F,Rocker_S_TNut_A,Rocker_S_TNut_F,LCBracket_AP_TNut_P,LCBracket_AP_TNut_A,LCBracket_AS_TNut_S,LCBracket_AS_TNut_A,+55 more]
  Origin = -> Origin
  Type = Assembly4 Model
---- part v5.6_Secondary.FCStd = doc fcstd_af7352a2449a (55458 chars; too large to inline — full recipe in that document) ----
